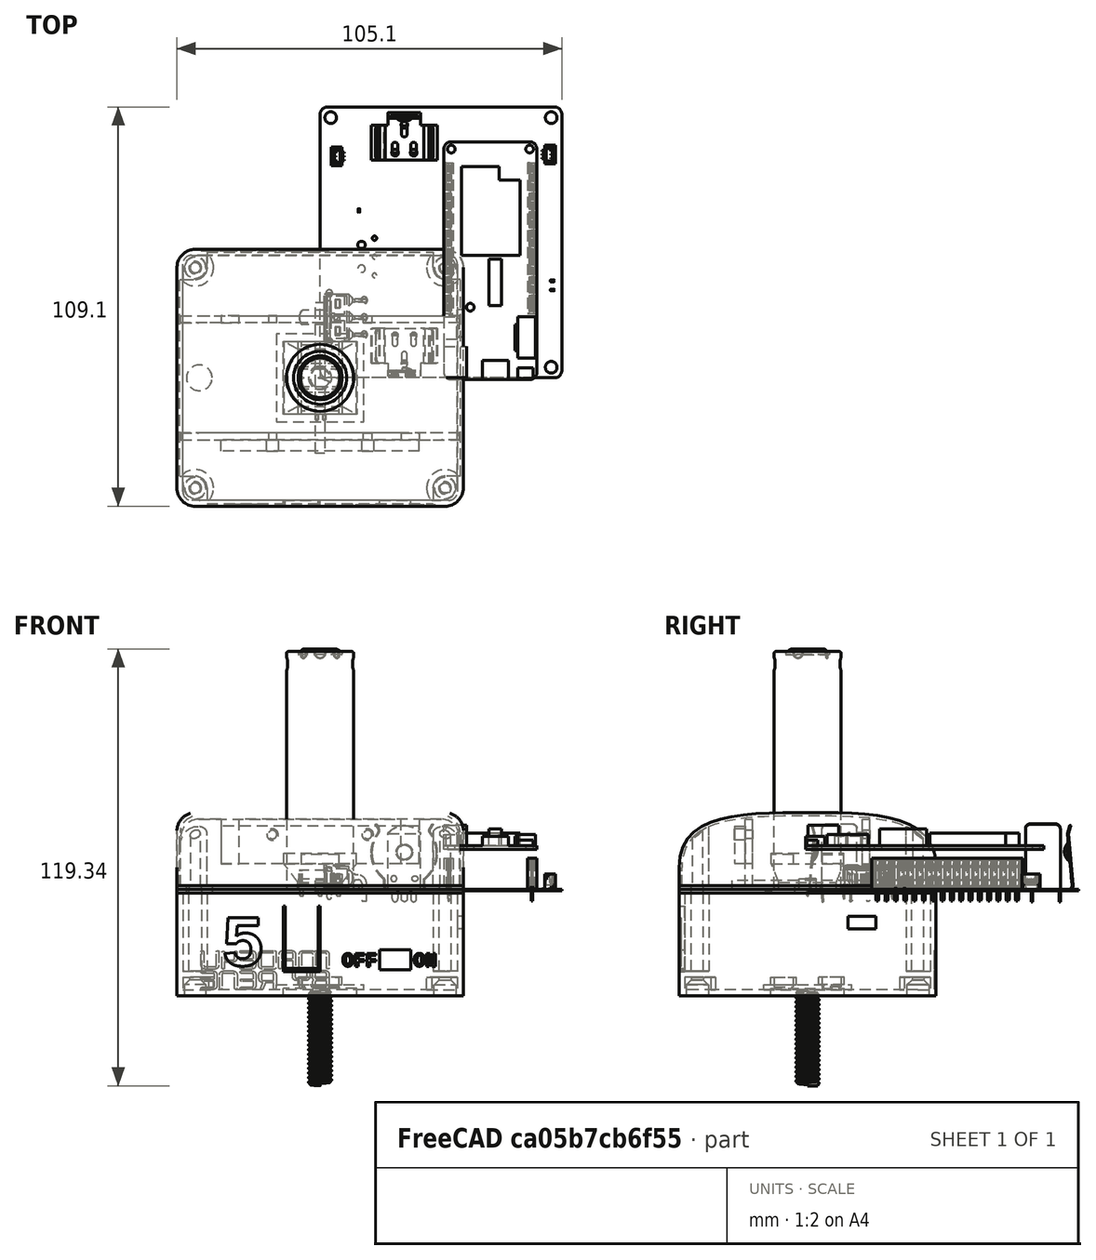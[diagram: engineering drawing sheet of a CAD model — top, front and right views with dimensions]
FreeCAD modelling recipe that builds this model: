
FCSTD DOCUMENT  (FreeCAD 0.20R29177 (Git))
Label: tally_light
License: All rights reserved
LicenseURL: http://en.wikipedia.org/wiki/All_rights_reserved
objects: Sketcher::SketchObject×40, PartDesign::Pocket×22, Part::Feature×20, App::Part×19, PartDesign::Mirrored×14, PartDesign::Pad×13, PartDesign::Body×11, PartDesign::MultiTransform×6, PartDesign::PolarPattern×4, PartDesign::Fillet×4, PartDesign::FeatureBase×2, Spreadsheet::Sheet×1, Mesh::Feature×1, App::DocumentObjectGroup×1, PartDesign::AdditiveLoft×1, Part::Cut×1, Part::MultiCommon×1, PartDesign::Chamfer×1, Part::MultiFuse×1, PartDesign::AdditiveHelix×1, +1 more types
note: 185 computed .brp shape members not serialized (recipe doc carries the construction recipe); baked Part::Feature solids carry a one-line shape summary decoded from their .brp

FEATURE [Spreadsheet::Sheet] Spreadsheet
  cells = A1=Width; B1(width)=78.2; A2=Depth; B2(depth)=70.2; A3=Height; B3(height)=50; A4=Wall Width; B4(wall_width)=1.6; A5=PCB Width; B5(pcb_width)=65; A6=PCB Depth; B6(pcb_depth)=25.6; A8=Light Wall Width; B8(light_wall_width)=0.8; A9=Light Height; B9(light_height)=20
FEATURE [Sketcher::SketchObject] Sketch002
  FullyConstrained = true
  MapMode = 5
  Support = -> [XY_Plane001]
  expr: Constraints[8] = Spreadsheet.depth
  expr: Constraints[9] = Spreadsheet.width
  sketch-geometry (4):
    g0: LineSegment StartX=-39.1 StartY=35.1 StartZ=0 EndX=39.1 EndY=35.1 EndZ=0
    g1: LineSegment StartX=39.1 StartY=35.1 StartZ=0 EndX=39.1 EndY=-35.1 EndZ=0
    g2: LineSegment StartX=39.1 StartY=-35.1 StartZ=0 EndX=-39.1 EndY=-35.1 EndZ=0
    g3: LineSegment StartX=-39.1 StartY=-35.1 StartZ=0 EndX=-39.1 EndY=35.1 EndZ=0
  constraints (11):
    c: Coincident(g0,g1)
    c: Coincident(g1,g2)
    c: Coincident(g2,g3)
    c: Coincident(g3,g0)
    c: Horizontal(g0)
    c: Horizontal(g2)
    c: Vertical(g1)
    c: Vertical(g3)
    c: Distance(g3) = 70.2
    c: Distance(g2) = 78.2
    c: Symmetric(g0,g2,g-1)
FEATURE [PartDesign::Pad] Pad001
  Direction = (0,0,1)
  Length = 1
  Length2 = 10
  Profile = -> Sketch002
  ReferenceAxis = -> Sketch002 [N_Axis]
  Type = 0
FEATURE [Sketcher::SketchObject] Sketch003
  AttachmentOffset = pos=(0,0,1) rot=(0,0,1;0rad)
  FullyConstrained = true
  MapMode = 5
  Placement = pos=(0,0,1) rot=(0,0,1;0rad)
  Support = -> [XY_Plane001]
  expr: Constraints[7] = Spreadsheet.width - 2 * Spreadsheet.light_wall_width - 0.4
  sketch-geometry (4):
    g0: LineSegment StartX=-38.1 StartY=17 StartZ=0 EndX=38.1 EndY=17 EndZ=0
    g1: LineSegment StartX=38.1 StartY=17 StartZ=0 EndX=38.1 EndY=15 EndZ=0
    g2: LineSegment StartX=38.1 StartY=15 StartZ=0 EndX=-38.1 EndY=15 EndZ=0
    g3: LineSegment StartX=-38.1 StartY=15 StartZ=0 EndX=-38.1 EndY=17 EndZ=0
  constraints (11):
    c: Coincident(g0,g1)
    c: Coincident(g1,g2)
    c: Coincident(g2,g3)
    c: Coincident(g3,g0)
    c: Vertical(g1)
    c: Vertical(g3)
    c: Distance(g3) = 2
    c: Distance(g0) = 76.2
    c: Symmetric(g2,g1,g-2)
    c: Distance(g-1,g2) = 15
    c: Horizontal(g0)
FEATURE [PartDesign::Pad] Pad002
  BaseFeature = -> Pad001
  Direction = (0,0,1)
  Length = 18.2
  Length2 = 10
  Profile = -> Sketch003
  ReferenceAxis = -> Sketch003 [N_Axis]
  Type = 0
  expr: Length = Spreadsheet.light_height - Spreadsheet.light_wall_width - 1
FEATURE [Sketcher::SketchObject] Sketch004
  FullyConstrained = true
  MapMode = 5
  Support = -> [XY_Plane002]
  expr: Constraints[17] = Spreadsheet.width
  expr: Constraints[18] = Spreadsheet.depth
  sketch-geometry (8):
    g0: LineSegment StartX=-34.1 StartY=35.1 StartZ=0 EndX=34.1 EndY=35.1 EndZ=0
    g1: LineSegment StartX=39.1 StartY=30.1 StartZ=0 EndX=39.1 EndY=-30.1 EndZ=0
    g2: LineSegment StartX=34.1 StartY=-35.1 StartZ=0 EndX=-34.1 EndY=-35.1 EndZ=0
    g3: LineSegment StartX=-39.1 StartY=-30.1 StartZ=0 EndX=-39.1 EndY=30.1 EndZ=0
    g4: ArcOfCircle CenterX=-34.1 CenterY=30.1 CenterZ=0 NormalX=0 NormalY=0 NormalZ=1 AngleXU=0 Radius=5 StartAngle=1.5708 EndAngle=3.14159
    g5: ArcOfCircle CenterX=34.1 CenterY=30.1 CenterZ=0 NormalX=0 NormalY=0 NormalZ=1 AngleXU=0 Radius=5 StartAngle=0 EndAngle=1.5708
    g6: ArcOfCircle CenterX=34.1 CenterY=-30.1 CenterZ=0 NormalX=0 NormalY=0 NormalZ=1 AngleXU=0 Radius=5 StartAngle=4.71239 EndAngle=6.28319
    g7: ArcOfCircle CenterX=-34.1 CenterY=-30.1 CenterZ=0 NormalX=0 NormalY=0 NormalZ=1 AngleXU=0 Radius=5 StartAngle=3.14159 EndAngle=4.71239
  constraints (19):
    c: Horizontal(g0)
    c: Vertical(g1)
    c: Horizontal(g2)
    c: Vertical(g3)
    c: Vertical(g0,g2)
    c: Vertical(g0,g2)
    c: Horizontal(g1,g3)
    c: Tangent(g2,g7) = 1.5708
    c: Tangent(g3,g7) = 1.5708
    c: Tangent(g0,g4) = 1.5708
    c: Tangent(g3,g4) = 1.5708
    c: Tangent(g0,g5) = 1.5708
    c: Tangent(g1,g5) = 1.5708
    c: Tangent(g1,g6) = 1.5708
    c: Tangent(g2,g6) = 1.5708
    c: Symmetric(g0,g2,g-1)
    c: Diameter(g4) = 10
    c: Distance(g3,g1) = 78.2
    c: Distance(g0,g2) = 70.2
FEATURE [PartDesign::Pad] Pad003
  Direction = (0,0,1)
  Length = 28
  Length2 = 10
  Profile = -> Sketch004
  ReferenceAxis = -> Sketch004 [N_Axis]
  Reversed = true
  Type = 0
  expr: Length = Spreadsheet.height - Spreadsheet.light_height - 2
FEATURE [Sketcher::SketchObject] Sketch006
  FullyConstrained = true
  MapMode = 5
  Support = -> [XY_Plane003]
  expr: Constraints[8] = Spreadsheet.depth
  expr: Constraints[9] = Spreadsheet.width
  sketch-geometry (4):
    g0: LineSegment StartX=-39.1 StartY=35.1 StartZ=0 EndX=39.1 EndY=35.1 EndZ=0
    g1: LineSegment StartX=39.1 StartY=35.1 StartZ=0 EndX=39.1 EndY=-35.1 EndZ=0
    g2: LineSegment StartX=39.1 StartY=-35.1 StartZ=0 EndX=-39.1 EndY=-35.1 EndZ=0
    g3: LineSegment StartX=-39.1 StartY=-35.1 StartZ=0 EndX=-39.1 EndY=35.1 EndZ=0
  constraints (11):
    c: Coincident(g0,g1)
    c: Coincident(g1,g2)
    c: Coincident(g2,g3)
    c: Coincident(g3,g0)
    c: Horizontal(g0)
    c: Horizontal(g2)
    c: Vertical(g1)
    c: Vertical(g3)
    c: Distance(g3) = 70.2
    c: Distance(g2) = 78.2
    c: Symmetric(g0,g2,g-1)
FEATURE [PartDesign::Pad] Pad004
  Direction = (0,0,1)
  Length = 1
  Length2 = 10
  Profile = -> Sketch006
  ReferenceAxis = -> Sketch006 [N_Axis]
  Reversed = true
  Type = 0
FEATURE [Sketcher::SketchObject] Sketch008
  AttachmentOffset = pos=(0,0,-28) rot=(0,0,1;0rad)
  ExternalGeometry = -> [Sketch004]
  FullyConstrained = true
  MapMode = 5
  Placement = pos=(0,0,-28) rot=(0,0,1;0rad)
  Support = -> [XY_Plane002]
  expr: .AttachmentOffset.Base.z = -(Spreadsheet.height - Spreadsheet.light_height - 2)
  sketch-geometry (2):
    g0: Circle CenterX=-34.1 CenterY=30.1 CenterZ=0 NormalX=0 NormalY=0 NormalZ=1 AngleXU=0 Radius=1.6
    g1: Circle CenterX=-34.1 CenterY=30.1 CenterZ=0 NormalX=0 NormalY=0 NormalZ=1 AngleXU=0 Radius=5
  constraints (5):
    c: Diameter(g0) = 3.2
    c: Coincident(g1,g0)
    c: Diameter(g1) = 10
    c: Distance(g-4,g0) = 5
    c: Distance(g0,g-3) = 5
FEATURE [Sketcher::SketchObject] Sketch009
  AttachmentOffset = pos=(0,0,-28) rot=(0,0,1;0rad)
  ExternalGeometry = -> [Pad003]
  FullyConstrained = true
  MapMode = 5
  Placement = pos=(0,0,-28) rot=(0,0,1;0rad)
  Support = -> [XY_Plane002]
  expr: .AttachmentOffset.Base.z = -(Spreadsheet.height - Spreadsheet.light_height) + 2
  sketch-geometry (1):
    g0: Circle CenterX=-34.1 CenterY=30.1 CenterZ=0 NormalX=0 NormalY=0 NormalZ=1 AngleXU=0 Radius=3
  constraints (3):
    c: Diameter(g0) = 6
    c: Distance(g-3,g0) = 5
    c: Distance(g-4,g0) = 5
FEATURE [Sketcher::SketchObject] Sketch010
  FullyConstrained = false
  MapMode = 5
  Support = -> [XY_Plane001]
  sketch-geometry (1):
    g0: Circle CenterX=-34.1 CenterY=30.1 CenterZ=0 NormalX=0 NormalY=0 NormalZ=1 AngleXU=0 Radius=1.6
  constraints (1):
    c: Diameter(g0) = 3.2
FEATURE [PartDesign::Mirrored] Mirrored007
  MirrorPlane = -> Sketch010 [V_Axis]
FEATURE [PartDesign::Mirrored] Mirrored008
  MirrorPlane = -> Sketch010 [H_Axis]
FEATURE [Sketcher::SketchObject] Sketch011
  FullyConstrained = false
  MapMode = 5
  Support = -> [XY_Plane003]
  sketch-geometry (1):
    g0: Circle CenterX=-34.1 CenterY=30.1 CenterZ=0 NormalX=0 NormalY=0 NormalZ=1 AngleXU=0 Radius=1.7
  constraints (1):
    c: Diameter(g0) = 3.4
FEATURE [PartDesign::Pocket] Pocket004
  BaseFeature = -> Pad004
  Direction = (0,0,-1)
  Length = 5
  Length2 = 5
  Midplane = true
  Profile = -> Sketch011
  ReferenceAxis = -> Sketch011 [N_Axis]
  Type = 1
FEATURE [PartDesign::Mirrored] Mirrored009
  MirrorPlane = -> Sketch011 [V_Axis]
FEATURE [PartDesign::Mirrored] Mirrored010
  MirrorPlane = -> Sketch011 [H_Axis]
FEATURE [PartDesign::MultiTransform] MultiTransform003
  BaseFeature = -> Pocket004
  Originals = -> [Pocket004]
  Transformations = -> [Mirrored009,Mirrored010]
FEATURE [Sketcher::SketchObject] Sketch013
  FullyConstrained = true
  MapMode = 5
  Support = -> [XY_Plane001]
  sketch-geometry (1):
    g0: Circle CenterX=-33 CenterY=0 CenterZ=0 NormalX=0 NormalY=0 NormalZ=1 AngleXU=0 Radius=3.5
  constraints (3):
    c: PointOnObject(g0,g-1)
    c: Diameter(g0) = 7
    c: Distance(g0,g-1) = 33
FEATURE [PartDesign::Mirrored] Mirrored011
  MirrorPlane = -> Sketch008 [V_Axis]
FEATURE [PartDesign::Mirrored] Mirrored012
  MirrorPlane = -> Sketch008 [H_Axis]
FEATURE [Sketcher::SketchObject] Sketch015
  FullyConstrained = true
  MapMode = 5
  Support = -> [XY_Plane003]
  expr: Constraints[12] = 5 - Spreadsheet.wall_width
  expr: Constraints[13] = 5 - Spreadsheet.wall_width
  expr: Constraints[14] = Spreadsheet.depth / 2 - 5
  expr: Constraints[15] = Spreadsheet.width / 2 - 5
  expr: Constraints[2] = 3.2 / 2 + Spreadsheet.wall_width
  sketch-geometry (6):
    g0: Circle CenterX=-34.1 CenterY=30.1 CenterZ=0 NormalX=0 NormalY=0 NormalZ=1 AngleXU=0 Radius=1.7
    g1: ArcOfCircle CenterX=-34.1 CenterY=30.1 CenterZ=0 NormalX=0 NormalY=0 NormalZ=1 AngleXU=0 Radius=3.2 StartAngle=4.71239 EndAngle=6.28319
    g2: LineSegment StartX=-30.9 StartY=33.5 StartZ=0 EndX=-37.5 EndY=33.5 EndZ=0
    g3: LineSegment StartX=-37.5 StartY=33.5 StartZ=0 EndX=-37.5 EndY=26.9 EndZ=0
    g4: LineSegment StartX=-30.9 StartY=30.1 StartZ=0 EndX=-30.9 EndY=33.5 EndZ=0
    g5: LineSegment StartX=-37.5 StartY=26.9 StartZ=0 EndX=-34.1 EndY=26.9 EndZ=0
  constraints (16):
    c: Diameter(g0) = 3.4
    c: Coincident(g1,g0)
    c: Radius(g1) = 3.2
    c: Horizontal(g2)
    c: Coincident(g3,g2)
    c: Vertical(g3)
    c: Coincident(g4,g2)
    c: Vertical(g4)
    c: Coincident(g5,g3)
    c: Horizontal(g5)
    c: Tangent(g4,g1) = -1.5708
    c: Tangent(g5,g1) = -1.5708
    c: Distance(g0,g2) = 3.4
    c: Distance(g0,g3) = 3.4
    c: Distance(g0,g-1) = 30.1
    c: Distance(g0,g-2) = 34.1
FEATURE [PartDesign::Pad] Pad008
  BaseFeature = -> MultiTransform003
  Direction = (0,0,1)
  Length = 22.3
  Length2 = 10
  Profile = -> Sketch015
  ReferenceAxis = -> Sketch015 [N_Axis]
  Reversed = true
  Type = 0
  expr: Length = Spreadsheet.height - Spreadsheet.light_height - 2 - 4 - 1.7
FEATURE [PartDesign::Mirrored] Mirrored017
  MirrorPlane = -> Sketch015 [V_Axis]
FEATURE [PartDesign::Mirrored] Mirrored018
  MirrorPlane = -> Sketch015 [H_Axis]
FEATURE [PartDesign::MultiTransform] MultiTransform006
  BaseFeature = -> Pad008
  Originals = -> [Pad008]
  Transformations = -> [Mirrored017,Mirrored018]
FEATURE [Sketcher::SketchObject] Sketch016
  FullyConstrained = true
  MapMode = 5
  Placement = pos=(0,-35.1,0) rot=(1,0,0;1.5708rad)
  Support = -> [Pad003]
  sketch-geometry (4):
    g0: LineSegment StartX=16.25 StartY=-15.5 StartZ=0 EndX=24.75 EndY=-15.5 EndZ=0
    g1: LineSegment StartX=24.75 StartY=-15.5 StartZ=0 EndX=24.75 EndY=-21 EndZ=0
    g2: LineSegment StartX=24.75 StartY=-21 StartZ=0 EndX=16.25 EndY=-21 EndZ=0
    g3: LineSegment StartX=16.25 StartY=-21 StartZ=0 EndX=16.25 EndY=-15.5 EndZ=0
  constraints (12):
    c: Coincident(g0,g1)
    c: Coincident(g1,g2)
    c: Coincident(g2,g3)
    c: Coincident(g3,g0)
    c: Horizontal(g0)
    c: Horizontal(g2)
    c: Vertical(g1)
    c: Vertical(g3)
    c: Distance(g1) = 5.5
    c: Distance(g2) = 8.5
    c: Distance(g0,g-2) = 16.25
    c: Distance(g0,g-1) = 15.5
FEATURE [Sketcher::SketchObject] Sketch017
  FullyConstrained = true
  MapMode = 5
  Placement = pos=(0,-35.1,0) rot=(1,0,0;1.5708rad)
  Support = -> [Pad003]
  sketch-geometry (8):
    g0: LineSegment StartX=-9.5 StartY=-3.5 StartZ=0 EndX=-10 EndY=-3.5 EndZ=0
    g1: LineSegment StartX=-10 StartY=-3.5 StartZ=0 EndX=-10 EndY=-21.5 EndZ=0
    g2: LineSegment StartX=-10 StartY=-21.5 StartZ=0 EndX=0 EndY=-21.5 EndZ=0
    g3: LineSegment StartX=0 StartY=-21.5 StartZ=0 EndX=0 EndY=-3.5 EndZ=0
    g4: LineSegment StartX=0 StartY=-3.5 StartZ=0 EndX=-0.5 EndY=-3.5 EndZ=0
    g5: LineSegment StartX=-0.5 StartY=-3.5 StartZ=0 EndX=-0.5 EndY=-20.5 EndZ=0
    g6: LineSegment StartX=-0.5 StartY=-20.5 StartZ=0 EndX=-9.5 EndY=-20.5 EndZ=0
    g7: LineSegment StartX=-9.5 StartY=-20.5 StartZ=0 EndX=-9.5 EndY=-3.5 EndZ=0
  constraints (24):
    c: Horizontal(g0)
    c: Coincident(g0,g1)
    c: Vertical(g1)
    c: Coincident(g1,g2)
    c: Horizontal(g2)
    c: Coincident(g2,g3)
    c: Vertical(g3)
    c: Coincident(g3,g4)
    c: Horizontal(g4)
    c: Coincident(g4,g5)
    c: Vertical(g5)
    c: Coincident(g5,g6)
    c: Horizontal(g6)
    c: Coincident(g6,g7)
    c: Coincident(g7,g0)
    c: Vertical(g7)
    c: Equal(g0,g4)
    c: Distance(g4) = 0.5
    c: Distance(g6,g2) = 1
    c: Horizontal(g4,g0)
    c: Distance(g5) = 17
    c: Distance(g3,g-1) = 3.5
    c: Distance(g2) = 10
    c: PointOnObject(g2,g-2)
FEATURE [Sketcher::SketchObject] Sketch018
  FullyConstrained = true
  MapMode = 5
  Placement = pos=(39.1,0,0) rot=(0.57735,0.57735,0.57735;2.0944rad)
  Support = -> [Pad003]
  sketch-geometry (4):
    g0: LineSegment StartX=11.1 StartY=-6.3 StartZ=0 EndX=18.6 EndY=-6.3 EndZ=0
    g1: LineSegment StartX=18.6 StartY=-6.3 StartZ=0 EndX=18.6 EndY=-9.8 EndZ=0
    g2: LineSegment StartX=18.6 StartY=-9.8 StartZ=0 EndX=11.1 EndY=-9.8 EndZ=0
    g3: LineSegment StartX=11.1 StartY=-9.8 StartZ=0 EndX=11.1 EndY=-6.3 EndZ=0
  constraints (12):
    c: Coincident(g0,g1)
    c: Coincident(g1,g2)
    c: Coincident(g2,g3)
    c: Coincident(g3,g0)
    c: Horizontal(g0)
    c: Horizontal(g2)
    c: Vertical(g1)
    c: Vertical(g3)
    c: Distance(g0) = 7.5
    c: Distance(g3) = 3.5
    c: Distance(g0,g-1) = 6.3
    c: Distance(g2,g-2) = 11.1
FEATURE [Sketcher::SketchObject] Sketch021
  FullyConstrained = true
  MapMode = 5
  Placement = pos=(0,0,0) rot=(1,0,0;1.5708rad)
  Support = -> [XZ_Plane001]
  expr: Constraints[2] = Spreadsheet.light_height / 2 + 10 / 2
  sketch-geometry (1):
    g0: Circle CenterX=-13 CenterY=15 CenterZ=0 NormalX=0 NormalY=0 NormalZ=1 AngleXU=0 Radius=1.15
  constraints (3):
    c: Diameter(g0) = 2.3
    c: Distance(g0,g-2) = 13
    c: Distance(g0,g-1) = 15
FEATURE [Part::Feature] Part__Feature001  label="Open CASCADE STEP translator 6.8 3.1.1"
  Placement = pos=(0,0,-0.41148) rot=(0,0,1;0rad)
  shape: bbox 66 x 74 x 0.4115 mm, 62 faces (baked)
FEATURE [App::Part] Board
  Group = -> [Part__Feature001]
  Origin = -> Origin004
FEATURE [Part::Feature] Part__Feature002  label="_____C161LFBN-RC"
  Placement = pos=(36.345,17.6,0) rot=(0.57735,0.57735,0.57735;2.0944rad)
  shape: bbox 2.54 x 41.14 x 11.7 mm, 810 faces, 17 solids (baked)
FEATURE [Part::Feature] Part__Feature003  label="_____C161LFBN-RC001"
  Placement = pos=(59.12,17.55,0) rot=(0.57735,0.57735,0.57735;2.0944rad)
  shape: bbox 2.54 x 41.14 x 11.7 mm, 810 faces, 17 solids (baked)
FEATURE [Part::Feature] Part__Feature004  label="wemos_d32_Pro"
  Placement = pos=(33.8,-0.5,11) rot=(0,0,1;0rad)
  shape: bbox 25.4 x 65 x 6.5 mm, 57 faces (baked)
FEATURE [Part::Feature] Part__Feature005  label="Extruded"
  shape: bbox 2.475 x 41.18 x 2.5 mm, 6 faces (baked)
FEATURE [App::Part] _465872176  label="8465872176"
  Group = -> [Part__Feature005]
  Origin = -> Origin005
  Placement = pos=(35.1875,38.1375,8.5) rot=(0,0,1;0rad)
FEATURE [Part::Feature] Part__Feature006  label="Extruded001"
  shape: bbox 2.475 x 41.18 x 2.5 mm, 6 faces (baked)
FEATURE [App::Part] _465872176001  label="8465872176001"
  Group = -> [Part__Feature006]
  Origin = -> Origin006
  Placement = pos=(57.8125,38.1375,8.5) rot=(0,0,1;0rad)
FEATURE [App::Part] U1
  Group = -> [Part__Feature002,Part__Feature003,Part__Feature004,_465872176,_465872176001]
  Origin = -> Origin007
FEATURE [Part::Feature] Part__Feature007  label="500SSPxS2M6xEA"
  Placement = pos=(7.9,16.5,3.3) rot=(-0.57735,-0.57735,0.57735;2.0944rad)
  shape: bbox 18.41 x 13.57 x 9.78 mm, 248 faces (baked)
FEATURE [App::Part] S2
  Group = -> [Part__Feature007]
  Origin = -> Origin008
FEATURE [Part::Feature] Part__Feature008  label="Open CASCADE STEP translator 6.8 3.4.1.1"
  shape: bbox 11.8 x 4.7 x 4.7 mm, 26 faces (baked)
FEATURE [Part::Feature] Part__Feature009  label="Open CASCADE STEP translator 6.8 3.4.1.2"
  shape: bbox 17.1 x 9.6 x 11.72 mm, 133 faces, 0 solids (baked)
FEATURE [App::Part] SS075xx02FxxxV2A
  Group = -> [Part__Feature008,Part__Feature009]
  Origin = -> Origin009
  Placement = pos=(9.75,33.045,2.875) rot=(-0.57735,-0.57735,0.57735;2.0944rad)
FEATURE [App::Part] S1
  Group = -> [SS075xx02FxxxV2A]
  Origin = -> Origin010
FEATURE [Part::Feature] Part__Feature010  label="RES0603"
  Placement = pos=(-0.899935,-10.6999,-0.41148) rot=(0.707107,0.707107,0;3.14159rad)
  shape: bbox 0.8002 x 1.6 x 0.45 mm, 22 faces, 4 solids (baked)
FEATURE [App::Part] R5
  Group = -> [Part__Feature010]
  Origin = -> Origin011
FEATURE [Part::Feature] Part__Feature011  label="RES0604"
  Placement = pos=(1.10007,-10.6999,-0.41148) rot=(0.707107,0.707107,0;3.14159rad)
  shape: bbox 0.8002 x 1.6 x 0.45 mm, 22 faces, 4 solids (baked)
FEATURE [App::Part] R4
  Group = -> [Part__Feature011]
  Origin = -> Origin012
FEATURE [Part::Feature] Part__Feature012  label="RES0402"
  Placement = pos=(63.3999,23.9999,0) rot=(0,0,1;3.14159rad)
  shape: bbox 1 x 0.5 x 0.3 mm, 22 faces, 4 solids (baked)
FEATURE [App::Part] R3
  Group = -> [Part__Feature012]
  Origin = -> Origin013
FEATURE [Part::Feature] Part__Feature013  label="RES0605"
  Placement = pos=(63.3999,26.4999,0) rot=(0,0,1;3.14159rad)
  shape: bbox 1 x 0.5 x 0.3 mm, 22 faces, 4 solids (baked)
FEATURE [App::Part] R2
  Group = -> [Part__Feature013]
  Origin = -> Origin014
FEATURE [Part::Feature] Part__Feature014  label="RES0606"
  Placement = pos=(10.5999,45.7001,0) rot=(0,0,1;1.5708rad)
  shape: bbox 0.5 x 1 x 0.3 mm, 22 faces, 4 solids (baked)
FEATURE [App::Part] R1
  Group = -> [Part__Feature014]
  Origin = -> Origin015
FEATURE [Part::Feature] Part__Feature015  label="BM03B-SRSS-TB"
  Placement = pos=(63.525,61.0001,0) rot=(0.57735,-0.57735,-0.57735;2.0944rad)
  shape: bbox 3.6 x 5 x 4.32 mm, 82 faces (baked)
FEATURE [App::Part] J2
  Group = -> [Part__Feature015]
  Origin = -> Origin016
FEATURE [Part::Feature] Part__Feature016  label="BM03B-SRSS-TB001"
  Placement = pos=(3.70004,60.4999,0) rot=(0.57735,0.57735,0.57735;2.0944rad)
  shape: bbox 3.6 x 5 x 4.32 mm, 82 faces (baked)
FEATURE [App::Part] J1
  Group = -> [Part__Feature016]
  Origin = -> Origin017
FEATURE [Part::Feature] Part__Feature017  label="keystone-PN54"
  Placement = pos=(23,13.5,0) rot=(0.57735,-0.57735,-0.57735;2.0944rad)
  shape: bbox 18.1 x 13.01 x 21.35 mm, 123 faces (baked)
FEATURE [Part::Feature] Part__Feature018  label="keystone-PN055"
  Placement = pos=(23,59.5,0) rot=(0.57735,0.57735,0.57735;2.0944rad)
  shape: bbox 18.1 x 13.01 x 21.35 mm, 123 faces (baked)
FEATURE [Part::Feature] Part__Feature019  label="Top_cover_v1"
  Placement = pos=(-1e-15,-2.09268e-05,65.7015) rot=(1,0,0;3.14159rad)
  shape: bbox 11.91 x 11.91 x 2.501 mm, 63 faces (baked)
FEATURE [Part::Feature] Part__Feature020  label="Open CASCADE STEP translator 6.8 3.12.3.2"
  shape: bbox 20.46 x 20.46 x 65 mm, 19 faces (baked)
FEATURE [App::Part] INR18650_35E  label="INR18650-35E"
  Group = -> [Part__Feature019,Part__Feature020]
  Origin = -> Origin018
  Placement = pos=(23,69,9.5) rot=(1,0,0;1.5708rad)
FEATURE [App::Part] BT1
  Group = -> [Part__Feature017,Part__Feature018,INR18650_35E]
  Origin = -> Origin019
FEATURE [App::Part] PCB  label="PCB001"
  Group = -> [Board,U1,S2,S1,R5,R4,R3,R2,R1,J2,J1,BT1]
  Origin = -> Origin020
  Placement = pos=(37,-33,-22.4) rot=(0,0,1;1.5708rad)
FEATURE [PartDesign::Mirrored] Mirrored013
  MirrorPlane = -> Sketch009 [V_Axis]
FEATURE [PartDesign::Mirrored] Mirrored014
  MirrorPlane = -> Sketch009 [H_Axis]
FEATURE [PartDesign::Mirrored] Mirrored023
  BaseFeature = -> Pad002
  MirrorPlane = -> Sketch003 [H_Axis]
  Originals = -> [Pad002]
FEATURE [PartDesign::Pocket] Pocket003
  BaseFeature = -> Mirrored023
  Direction = (0,0,-1)
  Length = 5
  Length2 = 5
  Midplane = true
  Profile = -> Sketch010
  ReferenceAxis = -> Sketch010 [N_Axis]
  Type = 1
FEATURE [PartDesign::MultiTransform] MultiTransform002
  BaseFeature = -> Pocket003
  Originals = -> [Pocket003]
  Transformations = -> [Mirrored007,Mirrored008]
FEATURE [PartDesign::Pocket] Pocket006
  BaseFeature = -> MultiTransform002
  Direction = (0,0,-1)
  Length = 5
  Length2 = 5
  Midplane = true
  Profile = -> Sketch013
  ReferenceAxis = -> Sketch013 [N_Axis]
  Type = 0
FEATURE [PartDesign::Pocket] Pocket012
  BaseFeature = -> Pocket006
  Direction = (0,1,2e-16)
  Length = 5
  Length2 = 5
  Midplane = true
  Profile = -> Sketch021
  ReferenceAxis = -> Sketch021 [N_Axis]
  Type = 1
FEATURE [Sketcher::SketchObject] Sketch023
  FullyConstrained = true
  MapMode = 5
  Support = -> [XY_Plane003]
  sketch-geometry (1):
    g0: Circle CenterX=-33 CenterY=0 CenterZ=0 NormalX=0 NormalY=0 NormalZ=1 AngleXU=0 Radius=3.5
  constraints (3):
    c: PointOnObject(g0,g-1)
    c: Diameter(g0) = 7
    c: Distance(g0,g-1) = 33
FEATURE [PartDesign::Pocket] Pocket014
  BaseFeature = -> MultiTransform006
  Direction = (0,0,-1)
  Length = 5
  Length2 = 5
  Profile = -> Sketch023
  ReferenceAxis = -> Sketch023 [N_Axis]
  Type = 0
FEATURE [PartDesign::Mirrored] Mirrored022
  BaseFeature = -> Pocket012
  MirrorPlane = -> Sketch021 [V_Axis]
  Originals = -> [Pocket012]
FEATURE [Sketcher::SketchObject] Sketch024
  FullyConstrained = true
  MapMode = 5
  Placement = pos=(0,0,0) rot=(1,0,0;1.5708rad)
  Support = -> [XZ_Plane001]
  expr: Constraints[8] = 54.2 / 2
  sketch-geometry (4):
    g0: LineSegment StartX=22.1 StartY=20 StartZ=0 EndX=27.1 EndY=20 EndZ=0
    g1: LineSegment StartX=27.1 StartY=20 StartZ=0 EndX=27.1 EndY=7 EndZ=0
    g2: LineSegment StartX=27.1 StartY=7 StartZ=0 EndX=22.1 EndY=7 EndZ=0
    g3: LineSegment StartX=22.1 StartY=7 StartZ=0 EndX=22.1 EndY=20 EndZ=0
  constraints (12):
    c: Coincident(g0,g1)
    c: Coincident(g1,g2)
    c: Coincident(g2,g3)
    c: Coincident(g3,g0)
    c: Horizontal(g0)
    c: Horizontal(g2)
    c: Vertical(g1)
    c: Vertical(g3)
    c: Distance(g0,g-2) = 27.1
    c: Distance(g0) = 5
    c: Distance(g1) = 13
    c: Distance(g0,g-1) = 20
FEATURE [PartDesign::Pocket] Pocket015
  BaseFeature = -> Mirrored022
  Direction = (0,1,2e-16)
  Length = 5
  Length2 = 5
  Profile = -> Sketch024
  ReferenceAxis = -> Sketch024 [N_Axis]
  Reversed = true
  Type = 1
FEATURE [PartDesign::PolarPattern] PolarPattern
  Angle = 360
  Axis = -> Sketch024 [V_Axis]
  BaseFeature = -> Pocket015
  Occurrences = 2
  Originals = -> [Pocket015]
FEATURE [Sketcher::SketchObject] Sketch025
  FullyConstrained = true
  MapMode = 5
  Placement = pos=(0,0,0) rot=(1,0,0;1.5708rad)
  Support = -> [XZ_Plane021]
  sketch-geometry (6):
    g0: LineSegment StartX=-27.1 StartY=5.05 StartZ=0 EndX=27.1 EndY=5.05 EndZ=0
    g1: LineSegment StartX=27.1 StartY=5.05 StartZ=0 EndX=27.1 EndY=-5.05 EndZ=0
    g2: LineSegment StartX=27.1 StartY=-5.05 StartZ=0 EndX=-27.1 EndY=-5.05 EndZ=0
    g3: LineSegment StartX=-27.1 StartY=-5.05 StartZ=0 EndX=-27.1 EndY=5.05 EndZ=0
    g4: Circle CenterX=-13 CenterY=2.75 CenterZ=0 NormalX=0 NormalY=0 NormalZ=1 AngleXU=0 Radius=1.55
    g5: Circle CenterX=13 CenterY=2.75 CenterZ=0 NormalX=0 NormalY=0 NormalZ=1 AngleXU=0 Radius=1.55
  constraints (16):
    c: Coincident(g0,g1)
    c: Coincident(g1,g2)
    c: Coincident(g2,g3)
    c: Coincident(g3,g0)
    c: Horizontal(g0)
    c: Horizontal(g2)
    c: Vertical(g1)
    c: Vertical(g3)
    c: Distance(g1) = 10.1
    c: Distance(g0) = 54.2
    c: Distance(g4,g2) = 7.8
    c: Diameter(g4) = 3.1
    c: Diameter(g5) = 3.1
    c: Distance(g5,g4) = 26
    c: Symmetric(g4,g5,g-2)
    c: Symmetric(g2,g0,g-1)
FEATURE [PartDesign::Pad] Pad010
  Direction = (0,-1,2e-16)
  Length = 3
  Length2 = 10
  Placement = pos=(0,0,0) rot=(1,0,0;1.5708rad)
  Profile = -> Sketch025
  ReferenceAxis = -> Sketch025 [N_Axis]
  Type = 0
FEATURE [PartDesign::Body] Body004  label="LEDFront"
  Group = -> [Sketch025,Pad010]
  Origin = -> Origin021
  Placement = pos=(0,20,12.25) rot=(0,0,1;0rad)
  Tip = -> Pad010
FEATURE [PartDesign::FeatureBase] Clone
  BaseFeature = -> Body004
  Placement = pos=(0,20,12.25) rot=(0,0,1;0rad)
FEATURE [PartDesign::Body] Body005  label="LEDBack"
  BaseFeature = -> Body004
  Group = -> [Clone]
  Origin = -> Origin022
  Placement = pos=(0,0,0) rot=(0,0,1;3.14159rad)
  Tip = -> Clone
FEATURE [Sketcher::SketchObject] Sketch026
  AttachmentOffset = pos=(0,0,-28) rot=(0,0,1;0rad)
  FullyConstrained = true
  MapMode = 5
  Placement = pos=(0,0,-28) rot=(0,0,1;0rad)
  Support = -> [XY_Plane002]
  expr: .AttachmentOffset.Base.z = -(Spreadsheet.height - Spreadsheet.light_height - 2)
  sketch-geometry (4):
    g0: LineSegment StartX=-12 StartY=12 StartZ=0 EndX=12 EndY=12 EndZ=0
    g1: LineSegment StartX=12 StartY=12 StartZ=0 EndX=12 EndY=-12 EndZ=0
    g2: LineSegment StartX=12 StartY=-12 StartZ=0 EndX=-12 EndY=-12 EndZ=0
    g3: LineSegment StartX=-12 StartY=-12 StartZ=0 EndX=-12 EndY=12 EndZ=0
  constraints (11):
    c: Coincident(g0,g1)
    c: Coincident(g1,g2)
    c: Coincident(g2,g3)
    c: Coincident(g3,g0)
    c: Horizontal(g0)
    c: Horizontal(g2)
    c: Vertical(g1)
    c: Vertical(g3)
    c: Equal(g0,g1)
    c: Symmetric(g0,g2,g-1)
    c: Distance(g1) = 24
FEATURE [Sketcher::SketchObject] Sketch027
  AttachmentOffset = pos=(0,0,-28) rot=(0,0,1;0rad)
  FullyConstrained = true
  MapMode = 5
  Placement = pos=(0,0,-28) rot=(0,0,1;0rad)
  Support = -> [XY_Plane002]
  expr: .AttachmentOffset.Base.z = -(Spreadsheet.height - Spreadsheet.light_height - 2)
  sketch-geometry (4):
    g0: LineSegment StartX=-10 StartY=10 StartZ=0 EndX=10 EndY=10 EndZ=0
    g1: LineSegment StartX=10 StartY=10 StartZ=0 EndX=10 EndY=-10 EndZ=0
    g2: LineSegment StartX=10 StartY=-10 StartZ=0 EndX=-10 EndY=-10 EndZ=0
    g3: LineSegment StartX=-10 StartY=-10 StartZ=0 EndX=-10 EndY=10 EndZ=0
  constraints (11):
    c: Coincident(g0,g1)
    c: Coincident(g1,g2)
    c: Coincident(g2,g3)
    c: Coincident(g3,g0)
    c: Horizontal(g0)
    c: Horizontal(g2)
    c: Vertical(g1)
    c: Vertical(g3)
    c: Equal(g0,g1)
    c: Symmetric(g0,g2,g-1)
    c: Distance(g1) = 20
FEATURE [Sketcher::SketchObject] Sketch028
  AttachmentOffset = pos=(0,0,-25) rot=(0,0,1;0rad)
  FullyConstrained = true
  MapMode = 5
  Placement = pos=(0,0,-25) rot=(0,0,1;0rad)
  Support = -> [XY_Plane002]
  expr: .AttachmentOffset.Base.z = -(Spreadsheet.height - Spreadsheet.light_height - 2) + 3
  sketch-geometry (4):
    g0: LineSegment StartX=-6 StartY=-3 StartZ=0 EndX=6 EndY=-3 EndZ=0
    g1: LineSegment StartX=6 StartY=-3 StartZ=0 EndX=6 EndY=-10 EndZ=0
    g2: LineSegment StartX=6 StartY=-10 StartZ=0 EndX=-6 EndY=-10 EndZ=0
    g3: LineSegment StartX=-6 StartY=-10 StartZ=0 EndX=-6 EndY=-3 EndZ=0
  constraints (11):
    c: Coincident(g0,g1)
    c: Coincident(g1,g2)
    c: Coincident(g2,g3)
    c: Coincident(g3,g0)
    c: Horizontal(g2)
    c: Vertical(g1)
    c: Vertical(g3)
    c: Distance(g1) = 7
    c: Distance(g-1,g2) = 10
    c: Distance(g0) = 12
    c: Symmetric(g0,g0,g-2)
FEATURE [Sketcher::SketchObject] Sketch029
  AttachmentOffset = pos=(0,0,-23) rot=(0,0,1;0rad)
  FullyConstrained = true
  MapMode = 5
  Placement = pos=(0,0,-23) rot=(0,0,1;0rad)
  Support = -> [XY_Plane002]
  expr: .AttachmentOffset.Base.z = -(Spreadsheet.height - Spreadsheet.light_height - 2) + 5
  sketch-geometry (4):
    g0: LineSegment StartX=-5.1 StartY=-3.9 StartZ=0 EndX=5.1 EndY=-3.9 EndZ=0
    g1: LineSegment StartX=5.1 StartY=-3.9 StartZ=0 EndX=5.1 EndY=-9.1 EndZ=0
    g2: LineSegment StartX=5.1 StartY=-9.1 StartZ=0 EndX=-5.1 EndY=-9.1 EndZ=0
    g3: LineSegment StartX=-5.1 StartY=-9.1 StartZ=0 EndX=-5.1 EndY=-3.9 EndZ=0
  constraints (11):
    c: Coincident(g0,g1)
    c: Coincident(g1,g2)
    c: Coincident(g2,g3)
    c: Coincident(g3,g0)
    c: Horizontal(g2)
    c: Vertical(g1)
    c: Vertical(g3)
    c: Distance(g1) = 5.2
    c: Distance(g-1,g2) = 9.1
    c: Distance(g0) = 10.2
    c: Symmetric(g0,g0,g-2)
FEATURE [Mesh::Feature] Sony_camera_flash_shoe_insert
  Placement = pos=(-10.5,8.85,-2) rot=(1,0,0;1.5708rad)
  expr: .Placement.Base.x = -21 / 2
  expr: .Placement.Base.y = 15.7 / 2 + 1
FEATURE [App::DocumentObjectGroup] Group  label="Electronics"
  Group = -> [PCB,Body004,Body005]
FEATURE [Sketcher::SketchObject] Sketch030
  FullyConstrained = true
  MapMode = 5
  Support = -> [XY_Plane025]
  sketch-geometry (4):
    g0: LineSegment StartX=-6.1 StartY=-7.85 StartZ=0 EndX=6.1 EndY=-7.85 EndZ=0
    g1: LineSegment StartX=6.1 StartY=-7.85 StartZ=0 EndX=6.1 EndY=7.85 EndZ=0
    g2: LineSegment StartX=6.1 StartY=7.85 StartZ=0 EndX=-6.1 EndY=7.85 EndZ=0
    g3: LineSegment StartX=-6.1 StartY=7.85 StartZ=0 EndX=-6.1 EndY=-7.85 EndZ=0
  constraints (11):
    c: Coincident(g0,g1)
    c: Coincident(g1,g2)
    c: Coincident(g2,g3)
    c: Coincident(g3,g0)
    c: Horizontal(g0)
    c: Horizontal(g2)
    c: Vertical(g1)
    c: Vertical(g3)
    c: Distance(g3) = 15.7
    c: Distance(g2) = 12.2
    c: Symmetric(g2,g0,g-1)
FEATURE [Sketcher::SketchObject] Sketch031
  AttachmentOffset = pos=(0,0,2) rot=(0,0,1;0rad)
  FullyConstrained = true
  MapMode = 5
  Placement = pos=(0,0,2) rot=(0,0,1;0rad)
  Support = -> [XY_Plane025]
  sketch-geometry (4):
    g0: LineSegment StartX=-6.1 StartY=-7.85 StartZ=0 EndX=6.1 EndY=-7.85 EndZ=0
    g1: LineSegment StartX=6.1 StartY=-7.85 StartZ=0 EndX=6.1 EndY=7.85 EndZ=0
    g2: LineSegment StartX=6.1 StartY=7.85 StartZ=0 EndX=-6.1 EndY=7.85 EndZ=0
    g3: LineSegment StartX=-6.1 StartY=7.85 StartZ=0 EndX=-6.1 EndY=-7.85 EndZ=0
  constraints (11):
    c: Coincident(g0,g1)
    c: Coincident(g1,g2)
    c: Coincident(g2,g3)
    c: Coincident(g3,g0)
    c: Horizontal(g0)
    c: Horizontal(g2)
    c: Vertical(g1)
    c: Vertical(g3)
    c: Distance(g3) = 15.7
    c: Distance(g2) = 12.2
    c: Symmetric(g2,g0,g-1)
FEATURE [Sketcher::SketchObject] Sketch032
  AttachmentOffset = pos=(0,0,7) rot=(0,0,1;0rad)
  FullyConstrained = true
  MapMode = 5
  Placement = pos=(0,0,7) rot=(0,0,1;0rad)
  Support = -> [XY_Plane025]
  sketch-geometry (4):
    g0: LineSegment StartX=-9.9 StartY=-9.9 StartZ=0 EndX=9.9 EndY=-9.9 EndZ=0
    g1: LineSegment StartX=9.9 StartY=-9.9 StartZ=0 EndX=9.9 EndY=9.9 EndZ=0
    g2: LineSegment StartX=9.9 StartY=9.9 StartZ=0 EndX=-9.9 EndY=9.9 EndZ=0
    g3: LineSegment StartX=-9.9 StartY=9.9 StartZ=0 EndX=-9.9 EndY=-9.9 EndZ=0
  constraints (11):
    c: Coincident(g0,g1)
    c: Coincident(g1,g2)
    c: Coincident(g2,g3)
    c: Coincident(g3,g0)
    c: Horizontal(g0)
    c: Horizontal(g2)
    c: Vertical(g1)
    c: Vertical(g3)
    c: Distance(g3) = 19.8
    c: Distance(g2) = 19.8
    c: Symmetric(g2,g0,g-1)
FEATURE [Sketcher::SketchObject] Sketch033
  AttachmentOffset = pos=(0,0,10) rot=(0,0,1;0rad)
  FullyConstrained = true
  MapMode = 5
  Placement = pos=(0,0,10) rot=(0,0,1;0rad)
  Support = -> [XY_Plane025]
  sketch-geometry (4):
    g0: LineSegment StartX=-9.9 StartY=-9.9 StartZ=0 EndX=9.9 EndY=-9.9 EndZ=0
    g1: LineSegment StartX=9.9 StartY=-9.9 StartZ=0 EndX=9.9 EndY=9.9 EndZ=0
    g2: LineSegment StartX=9.9 StartY=9.9 StartZ=0 EndX=-9.9 EndY=9.9 EndZ=0
    g3: LineSegment StartX=-9.9 StartY=9.9 StartZ=0 EndX=-9.9 EndY=-9.9 EndZ=0
  constraints (11):
    c: Coincident(g0,g1)
    c: Coincident(g1,g2)
    c: Coincident(g2,g3)
    c: Coincident(g3,g0)
    c: Horizontal(g0)
    c: Horizontal(g2)
    c: Vertical(g1)
    c: Vertical(g3)
    c: Distance(g3) = 19.8
    c: Distance(g2) = 19.8
    c: Symmetric(g2,g0,g-1)
FEATURE [PartDesign::AdditiveLoft] AdditiveLoft
  Closed = false
  Profile = -> Sketch030
  Ruled = true
  Sections = -> [Sketch031,Sketch032,Sketch033]
FEATURE [Sketcher::SketchObject] Sketch034
  AttachmentOffset = pos=(0,0,9.5) rot=(0,0,1;0rad)
  FullyConstrained = true
  MapMode = 5
  Placement = pos=(0,0,9.5) rot=(0,0,1;0rad)
  Support = -> [XY_Plane025]
  sketch-geometry (4):
    g0: LineSegment StartX=-5.1 StartY=-3.9 StartZ=0 EndX=5.1 EndY=-3.9 EndZ=0
    g1: LineSegment StartX=5.1 StartY=-3.9 StartZ=0 EndX=5.1 EndY=-19.1 EndZ=0
    g2: LineSegment StartX=5.1 StartY=-19.1 StartZ=0 EndX=-5.1 EndY=-19.1 EndZ=0
    g3: LineSegment StartX=-5.1 StartY=-19.1 StartZ=0 EndX=-5.1 EndY=-3.9 EndZ=0
  constraints (11):
    c: Coincident(g0,g1)
    c: Coincident(g1,g2)
    c: Coincident(g2,g3)
    c: Coincident(g3,g0)
    c: Horizontal(g2)
    c: Vertical(g1)
    c: Vertical(g3)
    c: Distance(g1) = 15.2
    c: Distance(g-1,g2) = 19.1
    c: Distance(g0) = 10.2
    c: Symmetric(g0,g0,g-2)
FEATURE [PartDesign::Pocket] Pocket018
  BaseFeature = -> AdditiveLoft
  Direction = (0,0,-1)
  Length = 2.5
  Length2 = 5
  Profile = -> Sketch034
  ReferenceAxis = -> Sketch034 [N_Axis]
  Type = 0
FEATURE [PartDesign::PolarPattern] PolarPattern003
  Angle = 360
  Axis = -> Sketch034 [N_Axis]
  BaseFeature = -> Pocket018
  Occurrences = 2
  Originals = -> [Pocket018]
FEATURE [PartDesign::Body] Body006  label="MagnetAdapter"
  Group = -> [Sketch030,Sketch031,Sketch032,AdditiveLoft,Sketch033,Sketch034,Pocket018,PolarPattern003]
  Origin = -> Origin025
  Tip = -> PolarPattern003
FEATURE [App::Part] Part001  label="HotShoeHolder"
  Group = -> [Body006,Sony_camera_flash_shoe_insert]
  Origin = -> Origin024
  Placement = pos=(0,0,-38) rot=(0,0,1;0rad)
FEATURE [Sketcher::SketchObject] Sketch035
  FullyConstrained = true
  MapMode = 5
  Placement = pos=(0,0,0) rot=(0.57735,0.57735,0.57735;2.0944rad)
  expr: Constraints[28] = Spreadsheet.light_height
  expr: Constraints[7] = Spreadsheet.depth
  sketch-geometry (12):
    g0: LineSegment StartX=-35.1 StartY=5 StartZ=0 EndX=-35.1 EndY=0 EndZ=0
    g1: LineSegment StartX=-35.1 StartY=0 StartZ=0 EndX=35.1 EndY=0 EndZ=0
    g2: LineSegment StartX=35.1 StartY=0 StartZ=0 EndX=35.1 EndY=5 EndZ=0
    g3-g7: Circle x5 (B-spline internal-alignment scaffolding for g8; pole/knot coordinates omitted)
    g8: BSplineCurve PolesCount=5 KnotsCount=3 Degree=3 IsPeriodic=0
    g9: GeomPoint X=-35.1 Y=5 Z=0
    g10: GeomPoint X=0 Y=20 Z=0
    g11: GeomPoint X=35.1 Y=5 Z=0
  constraints (26):
    c: PointOnObject(g0,g-1)
    c: Coincident(g0,g1)
    c: Coincident(g1,g2)
    c: Vertical(g2)
    c: Vertical(g0)
    c: Horizontal(g2,g0)
    c: Distance(g2) = 5
    c: Distance(g1) = 70.2
    c: Weight(g3) = 1
    c: Coincident(g8,g0)
    c: Equal(g3,g4)
    c: Equal(g3,g5)
    c: PointOnObject(g5,g-2)
    c: Equal(g3,g6)
    c: Equal(g3,g7)
    c: Coincident(g8,g2)
    c: InternalAlignment(g3-g7 -> g8) x5
    c: InternalAlignment(g9,g8)
    c: InternalAlignment(g10,g8)
    c: InternalAlignment(g11,g8)
    c: Vertical(g4,g0)
    c: Vertical(g6,g2)
    c: Horizontal(g6,g5)
    c: Horizontal(g5,g4)
    c: Distance(g5,g-1) = 20
    c: Symmetric(g0,g1,g-1)
FEATURE [PartDesign::Pad] Pad013
  Direction = (1,0,0)
  Length = 78.2
  Length2 = 10
  Midplane = true
  Placement = pos=(0,0,0) rot=(0.57735,0.57735,0.57735;2.0944rad)
  Profile = -> Sketch035
  ReferenceAxis = -> Sketch035 [N_Axis]
  Type = 0
  expr: Length = Spreadsheet.width
FEATURE [PartDesign::Fillet] Fillet
  Base = -> Pad013 [Edge12,Edge11]
  BaseFeature = -> Pad013
  Placement = pos=(0,0,0) rot=(0.57735,0.57735,0.57735;2.0944rad)
  Radius = 5
  SupportTransform = false
  UseAllEdges = false
FEATURE [PartDesign::Body] Body007  label="LightCoverOuter"
  Group = -> [Sketch035,Pad013,Fillet]
  Origin = -> Origin026
  Placement = pos=(0,0,1) rot=(0,0,1;0rad)
  Tip = -> Fillet
FEATURE [Sketcher::SketchObject] Sketch036
  FullyConstrained = true
  MapMode = 5
  Placement = pos=(0,0,0) rot=(0.57735,0.57735,0.57735;2.0944rad)
  expr: Constraints[28] = Spreadsheet.light_height - Spreadsheet.light_wall_width
  expr: Constraints[7] = Spreadsheet.depth - 2 * Spreadsheet.light_wall_width
  sketch-geometry (12):
    g0: LineSegment StartX=-34.3 StartY=5 StartZ=0 EndX=-34.3 EndY=0 EndZ=0
    g1: LineSegment StartX=-34.3 StartY=0 StartZ=0 EndX=34.3 EndY=0 EndZ=0
    g2: LineSegment StartX=34.3 StartY=0 StartZ=0 EndX=34.3 EndY=5 EndZ=0
    g3-g7: Circle x5 (B-spline internal-alignment scaffolding for g8; pole/knot coordinates omitted)
    g8: BSplineCurve PolesCount=5 KnotsCount=3 Degree=3 IsPeriodic=0
    g9: GeomPoint X=-34.3 Y=5 Z=0
    g10: GeomPoint X=0 Y=19.2 Z=0
    g11: GeomPoint X=34.3 Y=5 Z=0
  constraints (26):
    c: PointOnObject(g0,g-1)
    c: Coincident(g0,g1)
    c: Coincident(g1,g2)
    c: Vertical(g2)
    c: Vertical(g0)
    c: Horizontal(g2,g0)
    c: Distance(g2) = 5
    c: Distance(g1) = 68.6
    c: Weight(g3) = 1
    c: Coincident(g8,g0)
    c: Equal(g3,g4)
    c: Equal(g3,g5)
    c: PointOnObject(g5,g-2)
    c: Equal(g3,g6)
    c: Equal(g3,g7)
    c: Coincident(g8,g2)
    c: InternalAlignment(g3-g7 -> g8) x5
    c: InternalAlignment(g9,g8)
    c: InternalAlignment(g10,g8)
    c: InternalAlignment(g11,g8)
    c: Vertical(g4,g0)
    c: Vertical(g6,g2)
    c: Horizontal(g6,g5)
    c: Horizontal(g5,g4)
    c: Distance(g5,g-1) = 19.2
    c: Symmetric(g0,g1,g-1)
FEATURE [PartDesign::Pad] Pad014
  Direction = (1,0,0)
  Length = 76.6
  Length2 = 10
  Midplane = true
  Placement = pos=(0,0,0) rot=(0.57735,0.57735,0.57735;2.0944rad)
  Profile = -> Sketch036
  ReferenceAxis = -> Sketch036 [N_Axis]
  Type = 0
  expr: Length = Spreadsheet.width - 2 * Spreadsheet.light_wall_width
FEATURE [PartDesign::Fillet] Fillet001
  Base = -> Pad014 [Edge12,Edge11]
  BaseFeature = -> Pad014
  Placement = pos=(0,0,0) rot=(0.57735,0.57735,0.57735;2.0944rad)
  Radius = 5
  SupportTransform = false
  UseAllEdges = false
FEATURE [PartDesign::Body] Body008  label="LightCoverInner"
  Group = -> [Sketch036,Pad014,Fillet001]
  Origin = -> Origin027
  Placement = pos=(0,0,1) rot=(0,0,1;0rad)
  Tip = -> Fillet001
FEATURE [PartDesign::FeatureBase] Clone001
  BaseFeature = -> Body008
  Placement = pos=(0,0,1) rot=(0,0,1;0rad)
FEATURE [PartDesign::Body] Body009  label="LightCoverInnerCut"
  BaseFeature = -> Body008
  Group = -> [Clone001]
  Origin = -> Origin028
  Tip = -> Clone001
FEATURE [Part::Cut] Cut
  Base = -> Body007
  Tool = -> Body008
FEATURE [Sketcher::SketchObject] Sketch037
  FullyConstrained = true
  MapMode = 5
  Support = -> [XY_Plane027]
  expr: Constraints[10] = Spreadsheet.depth
  expr: Constraints[20] = Spreadsheet.light_wall_width
  expr: Constraints[21] = Spreadsheet.light_wall_width
  expr: Constraints[9] = Spreadsheet.width
  sketch-geometry (8):
    g0: LineSegment StartX=-39.1 StartY=35.1 StartZ=0 EndX=39.1 EndY=35.1 EndZ=0
    g1: LineSegment StartX=39.1 StartY=35.1 StartZ=0 EndX=39.1 EndY=-35.1 EndZ=0
    g2: LineSegment StartX=39.1 StartY=-35.1 StartZ=0 EndX=-39.1 EndY=-35.1 EndZ=0
    g3: LineSegment StartX=-39.1 StartY=-35.1 StartZ=0 EndX=-39.1 EndY=35.1 EndZ=0
    g4: LineSegment StartX=-38.3 StartY=34.3 StartZ=0 EndX=38.3 EndY=34.3 EndZ=0
    g5: LineSegment StartX=38.3 StartY=34.3 StartZ=0 EndX=38.3 EndY=-34.3 EndZ=0
    g6: LineSegment StartX=38.3 StartY=-34.3 StartZ=0 EndX=-38.3 EndY=-34.3 EndZ=0
    g7: LineSegment StartX=-38.3 StartY=-34.3 StartZ=0 EndX=-38.3 EndY=34.3 EndZ=0
  constraints (22):
    c: Coincident(g0,g1)
    c: Coincident(g1,g2)
    c: Coincident(g2,g3)
    c: Coincident(g3,g0)
    c: Horizontal(g0)
    c: Horizontal(g2)
    c: Vertical(g1)
    c: Vertical(g3)
    c: Symmetric(g1,g0,g-1)
    c: Distance(g0) = 78.2
    c: Distance(g1) = 70.2
    c: Coincident(g4,g5)
    c: Coincident(g5,g6)
    c: Coincident(g6,g7)
    c: Coincident(g7,g4)
    c: Horizontal(g4)
    c: Horizontal(g6)
    c: Vertical(g5)
    c: Vertical(g7)
    c: Symmetric(g4,g6,g-1)
    c: Distance(g4,g1) = 0.8
    c: Distance(g4,g0) = 0.8
FEATURE [PartDesign::Pad] Pad015
  Direction = (0,0,1)
  Length = 5
  Length2 = 10
  Profile = -> Sketch037
  ReferenceAxis = -> Sketch037 [N_Axis]
  Type = 0
FEATURE [Sketcher::SketchObject] Sketch038
  FullyConstrained = true
  MapMode = 5
  Support = -> [XY_Plane027]
  expr: Constraints[12] = 5 - Spreadsheet.light_wall_width
  expr: Constraints[13] = 5 - Spreadsheet.light_wall_width
  expr: Constraints[14] = Spreadsheet.depth / 2 - 5
  expr: Constraints[15] = Spreadsheet.width / 2 - 5
  expr: Constraints[2] = 3.2 / 2 + Spreadsheet.wall_width
  sketch-geometry (6):
    g0: Circle CenterX=-34.1 CenterY=30.1 CenterZ=0 NormalX=0 NormalY=0 NormalZ=1 AngleXU=0 Radius=1.4
    g1: ArcOfCircle CenterX=-34.1 CenterY=30.1 CenterZ=0 NormalX=0 NormalY=0 NormalZ=1 AngleXU=0 Radius=3.2 StartAngle=4.71239 EndAngle=6.28319
    g2: LineSegment StartX=-30.9 StartY=34.3 StartZ=0 EndX=-38.3 EndY=34.3 EndZ=0
    g3: LineSegment StartX=-38.3 StartY=34.3 StartZ=0 EndX=-38.3 EndY=26.9 EndZ=0
    g4: LineSegment StartX=-30.9 StartY=30.1 StartZ=0 EndX=-30.9 EndY=34.3 EndZ=0
    g5: LineSegment StartX=-38.3 StartY=26.9 StartZ=0 EndX=-34.1 EndY=26.9 EndZ=0
  constraints (16):
    c: Diameter(g0) = 2.8
    c: Coincident(g1,g0)
    c: Radius(g1) = 3.2
    c: Horizontal(g2)
    c: Coincident(g3,g2)
    c: Vertical(g3)
    c: Coincident(g4,g2)
    c: Vertical(g4)
    c: Coincident(g5,g3)
    c: Horizontal(g5)
    c: Tangent(g4,g1) = -1.5708
    c: Tangent(g5,g1) = -1.5708
    c: Distance(g0,g2) = 4.2
    c: Distance(g0,g3) = 4.2
    c: Distance(g0,g-1) = 30.1
    c: Distance(g0,g-2) = 34.1
FEATURE [PartDesign::Pad] Pad016
  BaseFeature = -> Pad015
  Direction = (0,0,1)
  Length = 20
  Length2 = 10
  Profile = -> Sketch038
  ReferenceAxis = -> Sketch038 [N_Axis]
  Type = 0
  expr: Length = Spreadsheet.light_height
FEATURE [PartDesign::Mirrored] Mirrored024
  MirrorPlane = -> Sketch038 [V_Axis]
FEATURE [PartDesign::Mirrored] Mirrored025
  MirrorPlane = -> Sketch038 [H_Axis]
FEATURE [PartDesign::MultiTransform] MultiTransform008
  BaseFeature = -> Pad016
  Originals = -> [Pad016]
  Transformations = -> [Mirrored024,Mirrored025]
FEATURE [PartDesign::Body] Body010
  Group = -> [Sketch037,Pad015,Sketch038,Pad016,MultiTransform008,Mirrored024,Mirrored025]
  Origin = -> Origin029
  Tip = -> MultiTransform008
FEATURE [Part::MultiCommon] Common
  Shapes = -> [Body010,Body009]
FEATURE [PartDesign::Fillet] Fillet002
  Base = -> PolarPattern [Edge58,Edge46,Edge5,Edge1,Edge2,Edge75,Edge8,Edge48]
  BaseFeature = -> PolarPattern
  Radius = 5
  SupportTransform = false
  UseAllEdges = false
FEATURE [PartDesign::Body] Body001  label="LedHolder"
  Group = -> [Sketch002,Pad001,Sketch003,Pad002,Mirrored023,Sketch010,Pocket003,MultiTransform002,Mirrored007,Mirrored008,Sketch013,Pocket006,Sketch021,Pocket012,Mirrored022,Sketch024,Pocket015,PolarPattern,Fillet002]
  Origin = -> Origin001
  Tip = -> Fillet002
FEATURE [PartDesign::Fillet] Fillet003
  Base = -> Pocket014 [Edge97,Edge2,Edge78,Edge8,Edge5,Edge67,Edge88,Edge1]
  BaseFeature = -> Pocket014
  Radius = 5
  SupportTransform = false
  UseAllEdges = false
FEATURE [PartDesign::Body] Body003  label="ElectronicsHolder"
  Group = -> [Sketch006,Pad004,Sketch011,Pocket004,MultiTransform003,Mirrored009,Mirrored010,Sketch015,Pad008,MultiTransform006,Mirrored017,Mirrored018,Sketch023,Pocket014,Fillet003]
  Origin = -> Origin003
  Tip = -> Fillet003
FEATURE [Sketcher::SketchObject] Sketch039
  FullyConstrained = true
  MapMode = 5
  Support = -> [XY_Plane002]
  expr: Constraints[17] = Spreadsheet.depth - 2 * Spreadsheet.wall_width
  expr: Constraints[18] = Spreadsheet.width - 2 * Spreadsheet.wall_width
  sketch-geometry (8):
    g0: LineSegment StartX=-32.5 StartY=33.5 StartZ=0 EndX=32.5 EndY=33.5 EndZ=0
    g1: LineSegment StartX=37.5 StartY=28.5 StartZ=0 EndX=37.5 EndY=-28.5 EndZ=0
    g2: LineSegment StartX=32.5 StartY=-33.5 StartZ=0 EndX=-32.5 EndY=-33.5 EndZ=0
    g3: LineSegment StartX=-37.5 StartY=-28.5 StartZ=0 EndX=-37.5 EndY=28.5 EndZ=0
    g4: ArcOfCircle CenterX=-32.5 CenterY=28.5 CenterZ=0 NormalX=0 NormalY=0 NormalZ=1 AngleXU=0 Radius=5 StartAngle=1.5708 EndAngle=3.14159
    g5: ArcOfCircle CenterX=32.5 CenterY=28.5 CenterZ=0 NormalX=0 NormalY=0 NormalZ=1 AngleXU=0 Radius=5 StartAngle=0 EndAngle=1.5708
    g6: ArcOfCircle CenterX=32.5 CenterY=-28.5 CenterZ=0 NormalX=0 NormalY=0 NormalZ=1 AngleXU=0 Radius=5 StartAngle=4.71239 EndAngle=6.28319
    g7: ArcOfCircle CenterX=-32.5 CenterY=-28.5 CenterZ=0 NormalX=0 NormalY=0 NormalZ=1 AngleXU=0 Radius=5 StartAngle=3.14159 EndAngle=4.71239
  constraints (19):
    c: Horizontal(g0)
    c: Vertical(g1)
    c: Horizontal(g2)
    c: Vertical(g3)
    c: Vertical(g0,g2)
    c: Vertical(g0,g2)
    c: Horizontal(g1,g3)
    c: Tangent(g2,g7) = 1.5708
    c: Tangent(g3,g7) = 1.5708
    c: Tangent(g0,g4) = 1.5708
    c: Tangent(g3,g4) = 1.5708
    c: Tangent(g0,g5) = 1.5708
    c: Tangent(g1,g5) = 1.5708
    c: Tangent(g1,g6) = 1.5708
    c: Tangent(g2,g6) = 1.5708
    c: Symmetric(g0,g2,g-1)
    c: Diameter(g4) = 10
    c: Distance(g0,g2) = 67
    c: Distance(g3,g1) = 75
FEATURE [PartDesign::Pocket] Pocket
  BaseFeature = -> Pad003
  Direction = (0,0,-1)
  Length = 0
  Length2 = 5
  Offset = -1.6
  Profile = -> Sketch039
  ReferenceAxis = -> Sketch039 [N_Axis]
  Type = 3
  UpToFace = -> Pad003 [Face10]
  expr: Offset = -Spreadsheet.wall_width
FEATURE [PartDesign::Pad] Pad006
  BaseFeature = -> Pocket
  Direction = (0,0,1)
  Length = 5
  Length2 = 10
  Profile = -> Sketch008
  ReferenceAxis = -> Sketch008 [N_Axis]
  Type = 0
FEATURE [PartDesign::MultiTransform] MultiTransform004
  BaseFeature = -> Pad006
  Originals = -> [Pad006]
  Transformations = -> [Mirrored011,Mirrored012]
FEATURE [PartDesign::Pocket] Pocket007
  BaseFeature = -> MultiTransform004
  Direction = (0,0,-1)
  Length = 3
  Length2 = 5
  Profile = -> Sketch009
  ReferenceAxis = -> Sketch009 [N_Axis]
  Reversed = true
  Type = 0
FEATURE [PartDesign::MultiTransform] MultiTransform
  BaseFeature = -> Pocket007
  Originals = -> [Pocket007]
  Transformations = -> [Mirrored013,Mirrored014]
FEATURE [PartDesign::Pocket] Pocket010
  BaseFeature = -> MultiTransform
  Direction = (-1,0,0)
  Length = 1.6
  Length2 = 5
  Profile = -> Sketch018
  ReferenceAxis = -> Sketch018 [N_Axis]
  Type = 0
  expr: Length = Spreadsheet.wall_width
FEATURE [PartDesign::Pocket] Pocket008
  BaseFeature = -> Pocket010
  Direction = (0,1,-2e-16)
  Length = 1.6
  Length2 = 5
  Profile = -> Sketch016
  ReferenceAxis = -> Sketch016 [N_Axis]
  Type = 0
  expr: Length = Spreadsheet.wall_width
FEATURE [PartDesign::Pocket] Pocket009
  BaseFeature = -> Pocket008
  Direction = (0,1,-2e-16)
  Length = 1.6
  Length2 = 5
  Profile = -> Sketch017
  ReferenceAxis = -> Sketch017 [N_Axis]
  Type = 0
  expr: Length = Spreadsheet.wall_width
FEATURE [PartDesign::Pad] Pad011
  BaseFeature = -> Pocket009
  Direction = (0,0,1)
  Length = 3
  Length2 = 10
  Profile = -> Sketch026
  ReferenceAxis = -> Sketch026 [N_Axis]
  Type = 0
FEATURE [PartDesign::Pocket] Pocket016
  BaseFeature = -> Pad011
  Direction = (0,0,-1)
  Length = 2
  Length2 = 5
  Profile = -> Sketch027
  ReferenceAxis = -> Sketch027 [N_Axis]
  Reversed = true
  Type = 0
FEATURE [PartDesign::Pad] Pad012
  BaseFeature = -> Pocket016
  Direction = (0,0,1)
  Length = 2
  Length2 = 10
  Profile = -> Sketch028
  ReferenceAxis = -> Sketch028 [N_Axis]
  Type = 0
FEATURE [PartDesign::PolarPattern] PolarPattern001
  Angle = 360
  Axis = -> Sketch028 [N_Axis]
  BaseFeature = -> Pad012
  Occurrences = 2
  Originals = -> [Pad012]
FEATURE [PartDesign::Pocket] Pocket017
  BaseFeature = -> PolarPattern001
  Direction = (0,0,-1)
  Length = 2.6
  Length2 = 5
  Profile = -> Sketch029
  ReferenceAxis = -> Sketch029 [N_Axis]
  Type = 0
FEATURE [PartDesign::PolarPattern] PolarPattern002
  Angle = 360
  Axis = -> Sketch029 [N_Axis]
  BaseFeature = -> Pocket017
  Occurrences = 2
  Originals = -> [Pocket017]
FEATURE [PartDesign::Chamfer] Chamfer
  Angle = 45
  Base = -> PolarPattern002 [Edge190,Edge189,Edge192,Edge202]
  BaseFeature = -> PolarPattern002
  ChamferType = 0
  FlipDirection = false
  Size = 1.3
  Size2 = 1
  SupportTransform = false
  UseAllEdges = false
FEATURE [Part::MultiFuse] Fusion  label="LightCover"
  Shapes = -> [Common,Cut]
FEATURE [Sketcher::SketchObject] Sketch
  FullyConstrained = true
  MapMode = 5
  Support = -> [XY_Plane002]
  expr: Constraints[15] = Spreadsheet.width - Spreadsheet.wall_width * 2
  expr: Constraints[16] = Spreadsheet.depth - Spreadsheet.wall_width * 2
  sketch-geometry (8):
    g0: LineSegment StartX=-35 StartY=33.5 StartZ=0 EndX=35 EndY=33.5 EndZ=0
    g1: LineSegment StartX=37.5 StartY=31 StartZ=0 EndX=37.5 EndY=-31 EndZ=0
    g2: LineSegment StartX=35 StartY=-33.5 StartZ=0 EndX=-35 EndY=-33.5 EndZ=0
    g3: LineSegment StartX=-37.5 StartY=-31 StartZ=0 EndX=-37.5 EndY=31 EndZ=0
    g4: ArcOfCircle CenterX=-35 CenterY=31 CenterZ=0 NormalX=0 NormalY=0 NormalZ=1 AngleXU=0 Radius=2.5 StartAngle=1.5708 EndAngle=3.14159
    g5: ArcOfCircle CenterX=35 CenterY=31 CenterZ=0 NormalX=0 NormalY=0 NormalZ=1 AngleXU=0 Radius=2.5 StartAngle=0 EndAngle=1.5708
    g6: ArcOfCircle CenterX=35 CenterY=-31 CenterZ=0 NormalX=0 NormalY=0 NormalZ=1 AngleXU=0 Radius=2.5 StartAngle=4.71239 EndAngle=6.28319
    g7: ArcOfCircle CenterX=-35 CenterY=-31 CenterZ=0 NormalX=0 NormalY=0 NormalZ=1 AngleXU=0 Radius=2.5 StartAngle=3.14159 EndAngle=4.71239
  constraints (19):
    c: Horizontal(g0)
    c: Vertical(g1)
    c: Horizontal(g2)
    c: Vertical(g3)
    c: Tangent(g3,g4) = 1.5708
    c: Tangent(g0,g4) = 1.5708
    c: Tangent(g0,g5) = 1.5708
    c: Tangent(g1,g5) = 1.5708
    c: Tangent(g1,g6) = 1.5708
    c: Tangent(g2,g6) = 1.5708
    c: Tangent(g2,g7) = 1.5708
    c: Tangent(g3,g7) = 1.5708
    c: Equal(g7,g6)
    c: Equal(g6,g5)
    c: Equal(g5,g4)
    c: Distance(g3,g1) = 75
    c: Distance(g0,g2) = 67
    c: Symmetric(g0,g2,g-1)
    c: Diameter(g4) = 5
FEATURE [PartDesign::Pocket] Pocket019
  BaseFeature = -> Chamfer
  Direction = (0,0,-1)
  Length = 23
  Length2 = 5
  Profile = -> Sketch
  ReferenceAxis = -> Sketch [N_Axis]
  Type = 0
FEATURE [Sketcher::SketchObject] Sketch040
  FullyConstrained = false
  Placement = pos=(0,-35.1,1) rot=(1,0,0;1.5708rad)
  expr: .Placement.Base.y = -Spreadsheet.depth / 2
  sketch-geometry (70):
    g0: BSplineCurve PolesCount=3 KnotsCount=2 Degree=2 IsPeriodic=0
    g1: BSplineCurve PolesCount=3 KnotsCount=2 Degree=2 IsPeriodic=0
    g2: BSplineCurve PolesCount=3 KnotsCount=2 Degree=2 IsPeriodic=0
    g3: BSplineCurve PolesCount=3 KnotsCount=2 Degree=2 IsPeriodic=0
    g4: BSplineCurve PolesCount=3 KnotsCount=2 Degree=2 IsPeriodic=0
    g5: BSplineCurve PolesCount=3 KnotsCount=2 Degree=2 IsPeriodic=0
    g6: BSplineCurve PolesCount=3 KnotsCount=2 Degree=2 IsPeriodic=0
    g7: BSplineCurve PolesCount=3 KnotsCount=2 Degree=2 IsPeriodic=0
    g8: BSplineCurve PolesCount=3 KnotsCount=2 Degree=2 IsPeriodic=0
    g9: BSplineCurve PolesCount=3 KnotsCount=2 Degree=2 IsPeriodic=0
    g10: BSplineCurve PolesCount=3 KnotsCount=2 Degree=2 IsPeriodic=0
    g11: BSplineCurve PolesCount=3 KnotsCount=2 Degree=2 IsPeriodic=0
    g12: BSplineCurve PolesCount=3 KnotsCount=2 Degree=2 IsPeriodic=0
    g13: BSplineCurve PolesCount=3 KnotsCount=2 Degree=2 IsPeriodic=0
    g14: BSplineCurve PolesCount=3 KnotsCount=2 Degree=2 IsPeriodic=0
    g15: BSplineCurve PolesCount=3 KnotsCount=2 Degree=2 IsPeriodic=0
    g16: LineSegment StartX=30.6345 StartY=-21 StartZ=0 EndX=29.6414 EndY=-18.3466 EndZ=0
    g17: LineSegment StartX=31.5293 StartY=-21 StartZ=0 EndX=30.6345 EndY=-21 EndZ=0
    g18: LineSegment StartX=31.5293 StartY=-17.469 StartZ=0 EndX=31.5293 EndY=-21 EndZ=0
    g19: LineSegment StartX=30.8655 StartY=-17.469 StartZ=0 EndX=31.5293 EndY=-17.469 EndZ=0
    g20: LineSegment StartX=30.8655 StartY=-19.2345 StartZ=0 EndX=30.8655 EndY=-17.469 EndZ=0
    g21: BSplineCurve PolesCount=3 KnotsCount=2 Degree=2 IsPeriodic=0
    g22: BSplineCurve PolesCount=3 KnotsCount=2 Degree=2 IsPeriodic=0
    g23: BSplineCurve PolesCount=3 KnotsCount=2 Degree=2 IsPeriodic=0
    g24: LineSegment StartX=29.9207 StartY=-17.469 StartZ=0 EndX=30.9379 EndY=-20.1931 EndZ=0
    g25: LineSegment StartX=29.05 StartY=-17.469 StartZ=0 EndX=29.9207 EndY=-17.469 EndZ=0
    g26: LineSegment StartX=29.05 StartY=-21 StartZ=0 EndX=29.05 EndY=-17.469 EndZ=0
    g27: LineSegment StartX=29.7138 StartY=-21 StartZ=0 EndX=29.05 EndY=-21 EndZ=0
    g28: LineSegment StartX=29.7138 StartY=-19.2759 StartZ=0 EndX=29.7138 EndY=-21 EndZ=0
    g29: BSplineCurve PolesCount=3 KnotsCount=2 Degree=2 IsPeriodic=0
    g30: BSplineCurve PolesCount=3 KnotsCount=2 Degree=2 IsPeriodic=0
    g31: BSplineCurve PolesCount=3 KnotsCount=2 Degree=2 IsPeriodic=0
    g32: BSplineCurve PolesCount=3 KnotsCount=2 Degree=2 IsPeriodic=0
    g33: BSplineCurve PolesCount=3 KnotsCount=2 Degree=2 IsPeriodic=0
    g34: BSplineCurve PolesCount=3 KnotsCount=2 Degree=2 IsPeriodic=0
    g35: BSplineCurve PolesCount=3 KnotsCount=2 Degree=2 IsPeriodic=0
    g36: BSplineCurve PolesCount=3 KnotsCount=2 Degree=2 IsPeriodic=0
    g37: BSplineCurve PolesCount=3 KnotsCount=2 Degree=2 IsPeriodic=0
    g38: BSplineCurve PolesCount=3 KnotsCount=2 Degree=2 IsPeriodic=0
    g39: BSplineCurve PolesCount=3 KnotsCount=2 Degree=2 IsPeriodic=0
    g40: BSplineCurve PolesCount=3 KnotsCount=2 Degree=2 IsPeriodic=0
    g41: BSplineCurve PolesCount=3 KnotsCount=2 Degree=2 IsPeriodic=0
    g42: BSplineCurve PolesCount=3 KnotsCount=2 Degree=2 IsPeriodic=0
    g43: BSplineCurve PolesCount=3 KnotsCount=2 Degree=2 IsPeriodic=0
    g44: BSplineCurve PolesCount=3 KnotsCount=2 Degree=2 IsPeriodic=0
    g45: BSplineCurve PolesCount=3 KnotsCount=2 Degree=2 IsPeriodic=0
    g46: BSplineCurve PolesCount=3 KnotsCount=2 Degree=2 IsPeriodic=0
    g47: BSplineCurve PolesCount=3 KnotsCount=2 Degree=2 IsPeriodic=0
    g48: BSplineCurve PolesCount=3 KnotsCount=2 Degree=2 IsPeriodic=0
    g49: BSplineCurve PolesCount=3 KnotsCount=2 Degree=2 IsPeriodic=0
    g50: LineSegment StartX=10.3948 StartY=-18.0207 StartZ=0 EndX=10.3948 EndY=-19.1241 EndZ=0
    g51: LineSegment StartX=12.0603 StartY=-18.0207 StartZ=0 EndX=10.3948 EndY=-18.0207 EndZ=0
    g52: LineSegment StartX=12.0603 StartY=-17.469 StartZ=0 EndX=12.0603 EndY=-18.0207 EndZ=0
    g53: LineSegment StartX=9.63276 StartY=-17.469 StartZ=0 EndX=12.0603 EndY=-17.469 EndZ=0
    g54: LineSegment StartX=9.63276 StartY=-21 StartZ=0 EndX=9.63276 EndY=-17.469 EndZ=0
    g55: LineSegment StartX=10.3948 StartY=-21 StartZ=0 EndX=9.63276 EndY=-21 EndZ=0
    g56: LineSegment StartX=10.3948 StartY=-19.6759 StartZ=0 EndX=10.3948 EndY=-21 EndZ=0
    g57: LineSegment StartX=12.0017 StartY=-19.6759 StartZ=0 EndX=10.3948 EndY=-19.6759 EndZ=0
    g58: LineSegment StartX=12.0017 StartY=-19.1241 StartZ=0 EndX=12.0017 EndY=-19.6759 EndZ=0
    g59: LineSegment StartX=10.3948 StartY=-19.1241 StartZ=0 EndX=12.0017 EndY=-19.1241 EndZ=0
    g60: LineSegment StartX=13.5948 StartY=-18.0207 StartZ=0 EndX=13.5948 EndY=-19.1241 EndZ=0
    g61: LineSegment StartX=15.2603 StartY=-18.0207 StartZ=0 EndX=13.5948 EndY=-18.0207 EndZ=0
    g62: LineSegment StartX=15.2603 StartY=-17.469 StartZ=0 EndX=15.2603 EndY=-18.0207 EndZ=0
    g63: LineSegment StartX=12.8328 StartY=-17.469 StartZ=0 EndX=15.2603 EndY=-17.469 EndZ=0
    g64: LineSegment StartX=12.8328 StartY=-21 StartZ=0 EndX=12.8328 EndY=-17.469 EndZ=0
    g65: LineSegment StartX=13.5948 StartY=-21 StartZ=0 EndX=12.8328 EndY=-21 EndZ=0
    g66: LineSegment StartX=13.5948 StartY=-19.6759 StartZ=0 EndX=13.5948 EndY=-21 EndZ=0
    g67: LineSegment StartX=15.2017 StartY=-19.6759 StartZ=0 EndX=13.5948 EndY=-19.6759 EndZ=0
    g68: LineSegment StartX=15.2017 StartY=-19.1241 StartZ=0 EndX=15.2017 EndY=-19.6759 EndZ=0
    g69: LineSegment StartX=13.5948 StartY=-19.1241 StartZ=0 EndX=15.2017 EndY=-19.1241 EndZ=0
  constraints (98):
    c: Coincident(g0,g1)
    c: Coincident(g1,g2)
    c: Coincident(g2,g3)
    c: Coincident(g3,g4)
    c: Coincident(g4,g5)
    c: Coincident(g5,g6)
    c: Coincident(g6,g7)
    c: Coincident(g7,g0)
    c: Coincident(g8,g9)
    c: Coincident(g9,g10)
    c: Coincident(g10,g11)
    c: Coincident(g11,g12)
    c: Coincident(g12,g13)
    c: Coincident(g13,g14)
    c: Coincident(g14,g15)
    c: Coincident(g15,g8)
    c: Coincident(g16,g17)
    c: Horizontal(g17)
    c: Coincident(g17,g18)
    c: Vertical(g18)
    c: Coincident(g18,g19)
    c: Horizontal(g19)
    c: Coincident(g19,g20)
    c: Vertical(g20)
    c: Coincident(g20,g21)
    c: Coincident(g21,g22)
    c: Coincident(g22,g23)
    c: Coincident(g23,g24)
    c: Coincident(g24,g25)
    c: Horizontal(g25)
    c: Coincident(g25,g26)
    c: Vertical(g26)
    c: Coincident(g26,g27)
    c: Horizontal(g27)
    c: Coincident(g27,g28)
    c: Vertical(g28)
    c: Coincident(g28,g29)
    c: Coincident(g29,g30)
    c: Coincident(g30,g31)
    c: Coincident(g31,g32)
    c: Coincident(g32,g33)
    c: Coincident(g33,g16)
    c: Coincident(g34,g35)
    c: Coincident(g35,g36)
    c: Coincident(g36,g37)
    c: Coincident(g37,g38)
    c: Coincident(g38,g39)
    c: Coincident(g39,g40)
    c: Coincident(g40,g41)
    c: Coincident(g41,g34)
    c: Coincident(g42,g43)
    c: Coincident(g43,g44)
    c: Coincident(g44,g45)
    c: Coincident(g45,g46)
    c: Coincident(g46,g47)
    c: Coincident(g47,g48)
    c: Coincident(g48,g49)
    c: Coincident(g49,g42)
    c: Vertical(g50)
    c: Coincident(g50,g51)
    c: Horizontal(g51)
    c: Coincident(g51,g52)
    c: Vertical(g52)
    c: Coincident(g52,g53)
    c: Horizontal(g53)
    c: Coincident(g53,g54)
    c: Vertical(g54)
    c: Coincident(g54,g55)
    c: Horizontal(g55)
    c: Coincident(g55,g56)
    c: Vertical(g56)
    c: Coincident(g56,g57)
    c: Horizontal(g57)
    c: Coincident(g57,g58)
    c: Vertical(g58)
    c: Coincident(g58,g59)
    c: Horizontal(g59)
    c: Coincident(g59,g50)
    c: Vertical(g60)
    c: Coincident(g60,g61)
    c: Horizontal(g61)
    c: Coincident(g61,g62)
    c: Vertical(g62)
    c: Coincident(g62,g63)
    c: Horizontal(g63)
    c: Coincident(g63,g64)
    c: Vertical(g64)
    c: Coincident(g64,g65)
    c: Horizontal(g65)
    c: Coincident(g65,g66)
    c: Vertical(g66)
    c: Coincident(g66,g67)
    c: Horizontal(g67)
    c: Coincident(g67,g68)
    c: Vertical(g68)
    c: Coincident(g68,g69)
    c: Horizontal(g69)
    c: Coincident(g69,g60)
FEATURE [PartDesign::Pocket] Pocket020
  BaseFeature = -> Pocket019
  Direction = (0,1,-2e-16)
  Length = 0.4
  Length2 = 5
  Profile = -> Sketch040
  ReferenceAxis = -> Sketch040 [N_Axis]
  Type = 0
FEATURE [Sketcher::SketchObject] Sketch041
  FullyConstrained = false
  Placement = pos=(-15,35.1,-21) rot=(0,0.707107,0.707107;3.14159rad)
  expr: .Placement.Base.y = Spreadsheet.depth / 2
  sketch-geometry (225):
    g0: BSplineCurve PolesCount=4 KnotsCount=2 Degree=3 IsPeriodic=0
    g1: BSplineCurve PolesCount=4 KnotsCount=2 Degree=3 IsPeriodic=0
    g2: BSplineCurve PolesCount=2 KnotsCount=2 Degree=1 IsPeriodic=0
    g3: BSplineCurve PolesCount=4 KnotsCount=2 Degree=3 IsPeriodic=0
    g4: BSplineCurve PolesCount=2 KnotsCount=2 Degree=1 IsPeriodic=0
    g5: BSplineCurve PolesCount=4 KnotsCount=2 Degree=3 IsPeriodic=0
    g6: BSplineCurve PolesCount=4 KnotsCount=2 Degree=3 IsPeriodic=0
    g7: BSplineCurve PolesCount=2 KnotsCount=2 Degree=1 IsPeriodic=0
    g8: BSplineCurve PolesCount=4 KnotsCount=2 Degree=3 IsPeriodic=0
    g9: BSplineCurve PolesCount=2 KnotsCount=2 Degree=1 IsPeriodic=0
    g10: BSplineCurve PolesCount=4 KnotsCount=2 Degree=3 IsPeriodic=0
    g11: BSplineCurve PolesCount=2 KnotsCount=2 Degree=1 IsPeriodic=0
    g12: BSplineCurve PolesCount=4 KnotsCount=2 Degree=3 IsPeriodic=0
    g13: BSplineCurve PolesCount=4 KnotsCount=2 Degree=3 IsPeriodic=0
    g14: BSplineCurve PolesCount=2 KnotsCount=2 Degree=1 IsPeriodic=0
    g15: BSplineCurve PolesCount=4 KnotsCount=2 Degree=3 IsPeriodic=0
    g16: BSplineCurve PolesCount=2 KnotsCount=2 Degree=1 IsPeriodic=0
    g17: BSplineCurve PolesCount=4 KnotsCount=2 Degree=3 IsPeriodic=0
    g18: BSplineCurve PolesCount=2 KnotsCount=2 Degree=1 IsPeriodic=0
    g19: BSplineCurve PolesCount=4 KnotsCount=2 Degree=3 IsPeriodic=0
    g20: BSplineCurve PolesCount=4 KnotsCount=2 Degree=3 IsPeriodic=0
    g21: BSplineCurve PolesCount=2 KnotsCount=2 Degree=1 IsPeriodic=0
    g22: BSplineCurve PolesCount=4 KnotsCount=2 Degree=3 IsPeriodic=0
    g23: BSplineCurve PolesCount=2 KnotsCount=2 Degree=1 IsPeriodic=0
    g24: BSplineCurve PolesCount=4 KnotsCount=2 Degree=3 IsPeriodic=0
    g25: BSplineCurve PolesCount=2 KnotsCount=2 Degree=1 IsPeriodic=0
    g26: BSplineCurve PolesCount=4 KnotsCount=2 Degree=3 IsPeriodic=0
    g27: BSplineCurve PolesCount=4 KnotsCount=2 Degree=3 IsPeriodic=0
    g28: BSplineCurve PolesCount=2 KnotsCount=2 Degree=1 IsPeriodic=0
    g29: BSplineCurve PolesCount=2 KnotsCount=2 Degree=1 IsPeriodic=0
    g30: BSplineCurve PolesCount=2 KnotsCount=2 Degree=1 IsPeriodic=0
    g31: BSplineCurve PolesCount=4 KnotsCount=2 Degree=3 IsPeriodic=0
    g32: BSplineCurve PolesCount=4 KnotsCount=2 Degree=3 IsPeriodic=0
    g33: BSplineCurve PolesCount=2 KnotsCount=2 Degree=1 IsPeriodic=0
    g34: BSplineCurve PolesCount=4 KnotsCount=2 Degree=3 IsPeriodic=0
    g35: BSplineCurve PolesCount=2 KnotsCount=2 Degree=1 IsPeriodic=0
    g36: BSplineCurve PolesCount=4 KnotsCount=2 Degree=3 IsPeriodic=0
    g37: BSplineCurve PolesCount=2 KnotsCount=2 Degree=1 IsPeriodic=0
    g38: BSplineCurve PolesCount=4 KnotsCount=2 Degree=3 IsPeriodic=0
    g39: BSplineCurve PolesCount=2 KnotsCount=2 Degree=1 IsPeriodic=0
    g40: BSplineCurve PolesCount=2 KnotsCount=2 Degree=1 IsPeriodic=0
    g41: BSplineCurve PolesCount=2 KnotsCount=2 Degree=1 IsPeriodic=0
    g42: BSplineCurve PolesCount=4 KnotsCount=2 Degree=3 IsPeriodic=0
    g43: BSplineCurve PolesCount=2 KnotsCount=2 Degree=1 IsPeriodic=0
    g44: BSplineCurve PolesCount=4 KnotsCount=2 Degree=3 IsPeriodic=0
    g45: BSplineCurve PolesCount=2 KnotsCount=2 Degree=1 IsPeriodic=0
    g46: BSplineCurve PolesCount=4 KnotsCount=2 Degree=3 IsPeriodic=0
    g47: BSplineCurve PolesCount=2 KnotsCount=2 Degree=1 IsPeriodic=0
    g48: BSplineCurve PolesCount=4 KnotsCount=2 Degree=3 IsPeriodic=0
    g49: BSplineCurve PolesCount=2 KnotsCount=2 Degree=1 IsPeriodic=0
    g50: BSplineCurve PolesCount=4 KnotsCount=2 Degree=3 IsPeriodic=0
    g51: BSplineCurve PolesCount=2 KnotsCount=2 Degree=1 IsPeriodic=0
    g52: BSplineCurve PolesCount=4 KnotsCount=2 Degree=3 IsPeriodic=0
    g53: BSplineCurve PolesCount=2 KnotsCount=2 Degree=1 IsPeriodic=0
    g54: BSplineCurve PolesCount=2 KnotsCount=2 Degree=1 IsPeriodic=0
    g55: BSplineCurve PolesCount=2 KnotsCount=2 Degree=1 IsPeriodic=0
    g56: BSplineCurve PolesCount=4 KnotsCount=2 Degree=3 IsPeriodic=0
    g57: BSplineCurve PolesCount=2 KnotsCount=2 Degree=1 IsPeriodic=0
    g58: BSplineCurve PolesCount=2 KnotsCount=2 Degree=1 IsPeriodic=0
    g59: BSplineCurve PolesCount=4 KnotsCount=2 Degree=3 IsPeriodic=0
    g60: BSplineCurve PolesCount=4 KnotsCount=2 Degree=3 IsPeriodic=0
    g61: BSplineCurve PolesCount=2 KnotsCount=2 Degree=1 IsPeriodic=0
    g62: BSplineCurve PolesCount=2 KnotsCount=2 Degree=1 IsPeriodic=0
    g63: BSplineCurve PolesCount=4 KnotsCount=2 Degree=3 IsPeriodic=0
    g64: BSplineCurve PolesCount=2 KnotsCount=2 Degree=1 IsPeriodic=0
    g65: BSplineCurve PolesCount=4 KnotsCount=2 Degree=3 IsPeriodic=0
    g66: BSplineCurve PolesCount=4 KnotsCount=2 Degree=3 IsPeriodic=0
    g67: BSplineCurve PolesCount=2 KnotsCount=2 Degree=1 IsPeriodic=0
    g68: BSplineCurve PolesCount=4 KnotsCount=2 Degree=3 IsPeriodic=0
    g69: BSplineCurve PolesCount=2 KnotsCount=2 Degree=1 IsPeriodic=0
    g70: BSplineCurve PolesCount=4 KnotsCount=2 Degree=3 IsPeriodic=0
    g71: BSplineCurve PolesCount=2 KnotsCount=2 Degree=1 IsPeriodic=0
    g72: BSplineCurve PolesCount=4 KnotsCount=2 Degree=3 IsPeriodic=0
    g73: BSplineCurve PolesCount=4 KnotsCount=2 Degree=3 IsPeriodic=0
    g74: BSplineCurve PolesCount=2 KnotsCount=2 Degree=1 IsPeriodic=0
    g75: BSplineCurve PolesCount=2 KnotsCount=2 Degree=1 IsPeriodic=0
    g76: BSplineCurve PolesCount=4 KnotsCount=2 Degree=3 IsPeriodic=0
    g77: BSplineCurve PolesCount=2 KnotsCount=2 Degree=1 IsPeriodic=0
    g78: BSplineCurve PolesCount=4 KnotsCount=2 Degree=3 IsPeriodic=0
    g79: BSplineCurve PolesCount=2 KnotsCount=2 Degree=1 IsPeriodic=0
    g80: BSplineCurve PolesCount=4 KnotsCount=2 Degree=3 IsPeriodic=0
    g81: BSplineCurve PolesCount=4 KnotsCount=2 Degree=3 IsPeriodic=0
    g82: BSplineCurve PolesCount=2 KnotsCount=2 Degree=1 IsPeriodic=0
    g83: BSplineCurve PolesCount=4 KnotsCount=2 Degree=3 IsPeriodic=0
    g84: BSplineCurve PolesCount=2 KnotsCount=2 Degree=1 IsPeriodic=0
    g85: BSplineCurve PolesCount=4 KnotsCount=2 Degree=3 IsPeriodic=0
    g86: BSplineCurve PolesCount=2 KnotsCount=2 Degree=1 IsPeriodic=0
    g87: BSplineCurve PolesCount=4 KnotsCount=2 Degree=3 IsPeriodic=0
    g88: BSplineCurve PolesCount=4 KnotsCount=2 Degree=3 IsPeriodic=0
    g89: BSplineCurve PolesCount=2 KnotsCount=2 Degree=1 IsPeriodic=0
    g90: BSplineCurve PolesCount=4 KnotsCount=2 Degree=3 IsPeriodic=0
    g91: BSplineCurve PolesCount=4 KnotsCount=2 Degree=3 IsPeriodic=0
    g92: BSplineCurve PolesCount=4 KnotsCount=2 Degree=3 IsPeriodic=0
    g93: BSplineCurve PolesCount=2 KnotsCount=2 Degree=1 IsPeriodic=0
    g94: BSplineCurve PolesCount=4 KnotsCount=2 Degree=3 IsPeriodic=0
    g95: BSplineCurve PolesCount=2 KnotsCount=2 Degree=1 IsPeriodic=0
    g96: BSplineCurve PolesCount=4 KnotsCount=2 Degree=3 IsPeriodic=0
    g97: BSplineCurve PolesCount=4 KnotsCount=2 Degree=3 IsPeriodic=0
    g98: BSplineCurve PolesCount=2 KnotsCount=2 Degree=1 IsPeriodic=0
    g99: BSplineCurve PolesCount=4 KnotsCount=2 Degree=3 IsPeriodic=0
    g100: BSplineCurve PolesCount=2 KnotsCount=2 Degree=1 IsPeriodic=0
    g101: BSplineCurve PolesCount=4 KnotsCount=2 Degree=3 IsPeriodic=0
    g102: BSplineCurve PolesCount=2 KnotsCount=2 Degree=1 IsPeriodic=0
    g103: BSplineCurve PolesCount=4 KnotsCount=2 Degree=3 IsPeriodic=0
    g104: BSplineCurve PolesCount=4 KnotsCount=2 Degree=3 IsPeriodic=0
    g105: BSplineCurve PolesCount=2 KnotsCount=2 Degree=1 IsPeriodic=0
    g106: BSplineCurve PolesCount=4 KnotsCount=2 Degree=3 IsPeriodic=0
    g107: BSplineCurve PolesCount=2 KnotsCount=2 Degree=1 IsPeriodic=0
    g108: BSplineCurve PolesCount=4 KnotsCount=2 Degree=3 IsPeriodic=0
    g109: BSplineCurve PolesCount=2 KnotsCount=2 Degree=1 IsPeriodic=0
    g110: BSplineCurve PolesCount=4 KnotsCount=2 Degree=3 IsPeriodic=0
    g111: BSplineCurve PolesCount=2 KnotsCount=2 Degree=1 IsPeriodic=0
    g112: BSplineCurve PolesCount=4 KnotsCount=2 Degree=3 IsPeriodic=0
    g113: BSplineCurve PolesCount=4 KnotsCount=2 Degree=3 IsPeriodic=0
    g114: BSplineCurve PolesCount=2 KnotsCount=2 Degree=1 IsPeriodic=0
    g115: BSplineCurve PolesCount=4 KnotsCount=2 Degree=3 IsPeriodic=0
    g116: BSplineCurve PolesCount=2 KnotsCount=2 Degree=1 IsPeriodic=0
    g117: BSplineCurve PolesCount=2 KnotsCount=2 Degree=1 IsPeriodic=0
    g118: BSplineCurve PolesCount=4 KnotsCount=2 Degree=3 IsPeriodic=0
    g119: BSplineCurve PolesCount=2 KnotsCount=2 Degree=1 IsPeriodic=0
    g120: BSplineCurve PolesCount=4 KnotsCount=2 Degree=3 IsPeriodic=0
    g121: BSplineCurve PolesCount=2 KnotsCount=2 Degree=1 IsPeriodic=0
    g122: BSplineCurve PolesCount=4 KnotsCount=2 Degree=3 IsPeriodic=0
    g123: BSplineCurve PolesCount=2 KnotsCount=2 Degree=1 IsPeriodic=0
    g124: BSplineCurve PolesCount=2 KnotsCount=2 Degree=1 IsPeriodic=0
    g125: BSplineCurve PolesCount=2 KnotsCount=2 Degree=1 IsPeriodic=0
    g126: BSplineCurve PolesCount=4 KnotsCount=2 Degree=3 IsPeriodic=0
    g127: BSplineCurve PolesCount=2 KnotsCount=2 Degree=1 IsPeriodic=0
    g128: BSplineCurve PolesCount=4 KnotsCount=2 Degree=3 IsPeriodic=0
    g129: BSplineCurve PolesCount=2 KnotsCount=2 Degree=1 IsPeriodic=0
    g130: BSplineCurve PolesCount=4 KnotsCount=2 Degree=3 IsPeriodic=0
    g131: BSplineCurve PolesCount=2 KnotsCount=2 Degree=1 IsPeriodic=0
    g132: BSplineCurve PolesCount=4 KnotsCount=2 Degree=3 IsPeriodic=0
    g133: BSplineCurve PolesCount=2 KnotsCount=2 Degree=1 IsPeriodic=0
    g134: BSplineCurve PolesCount=4 KnotsCount=2 Degree=3 IsPeriodic=0
    g135: BSplineCurve PolesCount=2 KnotsCount=2 Degree=1 IsPeriodic=0
    g136: BSplineCurve PolesCount=4 KnotsCount=2 Degree=3 IsPeriodic=0
    g137: BSplineCurve PolesCount=4 KnotsCount=2 Degree=3 IsPeriodic=0
    g138: BSplineCurve PolesCount=2 KnotsCount=2 Degree=1 IsPeriodic=0
    g139: BSplineCurve PolesCount=4 KnotsCount=2 Degree=3 IsPeriodic=0
    g140: BSplineCurve PolesCount=2 KnotsCount=2 Degree=1 IsPeriodic=0
    g141: BSplineCurve PolesCount=2 KnotsCount=2 Degree=1 IsPeriodic=0
    g142: BSplineCurve PolesCount=4 KnotsCount=2 Degree=3 IsPeriodic=0
    g143: BSplineCurve PolesCount=4 KnotsCount=2 Degree=3 IsPeriodic=0
    g144: BSplineCurve PolesCount=2 KnotsCount=2 Degree=1 IsPeriodic=0
    g145: BSplineCurve PolesCount=2 KnotsCount=2 Degree=1 IsPeriodic=0
    g146: BSplineCurve PolesCount=4 KnotsCount=2 Degree=3 IsPeriodic=0
    g147: BSplineCurve PolesCount=2 KnotsCount=2 Degree=1 IsPeriodic=0
    g148: BSplineCurve PolesCount=4 KnotsCount=2 Degree=3 IsPeriodic=0
    g149: BSplineCurve PolesCount=2 KnotsCount=2 Degree=1 IsPeriodic=0
    g150: BSplineCurve PolesCount=4 KnotsCount=2 Degree=3 IsPeriodic=0
    g151: BSplineCurve PolesCount=2 KnotsCount=2 Degree=1 IsPeriodic=0
    g152: BSplineCurve PolesCount=4 KnotsCount=2 Degree=3 IsPeriodic=0
    g153: BSplineCurve PolesCount=4 KnotsCount=2 Degree=3 IsPeriodic=0
    g154: BSplineCurve PolesCount=2 KnotsCount=2 Degree=1 IsPeriodic=0
    g155: BSplineCurve PolesCount=2 KnotsCount=2 Degree=1 IsPeriodic=0
    g156: BSplineCurve PolesCount=2 KnotsCount=2 Degree=1 IsPeriodic=0
    g157: BSplineCurve PolesCount=4 KnotsCount=2 Degree=3 IsPeriodic=0
    g158: BSplineCurve PolesCount=4 KnotsCount=2 Degree=3 IsPeriodic=0
    g159: BSplineCurve PolesCount=4 KnotsCount=2 Degree=3 IsPeriodic=0
    g160: BSplineCurve PolesCount=4 KnotsCount=2 Degree=3 IsPeriodic=0
    g161: BSplineCurve PolesCount=4 KnotsCount=2 Degree=3 IsPeriodic=0
    g162: BSplineCurve PolesCount=4 KnotsCount=2 Degree=3 IsPeriodic=0
    g163: BSplineCurve PolesCount=2 KnotsCount=2 Degree=1 IsPeriodic=0
    g164: BSplineCurve PolesCount=4 KnotsCount=2 Degree=3 IsPeriodic=0
    g165: BSplineCurve PolesCount=2 KnotsCount=2 Degree=1 IsPeriodic=0
    g166: BSplineCurve PolesCount=4 KnotsCount=2 Degree=3 IsPeriodic=0
    g167: BSplineCurve PolesCount=2 KnotsCount=2 Degree=1 IsPeriodic=0
    g168: BSplineCurve PolesCount=2 KnotsCount=2 Degree=1 IsPeriodic=0
    g169: BSplineCurve PolesCount=4 KnotsCount=2 Degree=3 IsPeriodic=0
    g170: BSplineCurve PolesCount=2 KnotsCount=2 Degree=1 IsPeriodic=0
    g171: BSplineCurve PolesCount=4 KnotsCount=2 Degree=3 IsPeriodic=0
    g172: BSplineCurve PolesCount=2 KnotsCount=2 Degree=1 IsPeriodic=0
    g173: BSplineCurve PolesCount=4 KnotsCount=2 Degree=3 IsPeriodic=0
    g174: BSplineCurve PolesCount=2 KnotsCount=2 Degree=1 IsPeriodic=0
    g175: BSplineCurve PolesCount=2 KnotsCount=2 Degree=1 IsPeriodic=0
    g176: BSplineCurve PolesCount=4 KnotsCount=2 Degree=3 IsPeriodic=0
    g177: BSplineCurve PolesCount=4 KnotsCount=2 Degree=3 IsPeriodic=0
    g178: BSplineCurve PolesCount=2 KnotsCount=2 Degree=1 IsPeriodic=0
    g179: BSplineCurve PolesCount=2 KnotsCount=2 Degree=1 IsPeriodic=0
    g180: BSplineCurve PolesCount=4 KnotsCount=2 Degree=3 IsPeriodic=0
    g181: BSplineCurve PolesCount=2 KnotsCount=2 Degree=1 IsPeriodic=0
    g182: BSplineCurve PolesCount=4 KnotsCount=2 Degree=3 IsPeriodic=0
    g183: BSplineCurve PolesCount=4 KnotsCount=2 Degree=3 IsPeriodic=0
    g184: BSplineCurve PolesCount=2 KnotsCount=2 Degree=1 IsPeriodic=0
    g185: BSplineCurve PolesCount=4 KnotsCount=2 Degree=3 IsPeriodic=0
    g186: BSplineCurve PolesCount=2 KnotsCount=2 Degree=1 IsPeriodic=0
    g187: BSplineCurve PolesCount=4 KnotsCount=2 Degree=3 IsPeriodic=0
    g188: BSplineCurve PolesCount=2 KnotsCount=2 Degree=1 IsPeriodic=0
    g189: BSplineCurve PolesCount=4 KnotsCount=2 Degree=3 IsPeriodic=0
    g190: BSplineCurve PolesCount=4 KnotsCount=2 Degree=3 IsPeriodic=0
    g191: BSplineCurve PolesCount=2 KnotsCount=2 Degree=1 IsPeriodic=0
    g192: BSplineCurve PolesCount=4 KnotsCount=2 Degree=3 IsPeriodic=0
    g193: BSplineCurve PolesCount=4 KnotsCount=2 Degree=3 IsPeriodic=0
    g194: BSplineCurve PolesCount=2 KnotsCount=2 Degree=1 IsPeriodic=0
    g195: BSplineCurve PolesCount=4 KnotsCount=2 Degree=3 IsPeriodic=0
    g196: BSplineCurve PolesCount=2 KnotsCount=2 Degree=1 IsPeriodic=0
    g197: BSplineCurve PolesCount=4 KnotsCount=2 Degree=3 IsPeriodic=0
    g198: BSplineCurve PolesCount=2 KnotsCount=2 Degree=1 IsPeriodic=0
    g199: BSplineCurve PolesCount=4 KnotsCount=2 Degree=3 IsPeriodic=0
    g200: BSplineCurve PolesCount=4 KnotsCount=2 Degree=3 IsPeriodic=0
    g201: BSplineCurve PolesCount=2 KnotsCount=2 Degree=1 IsPeriodic=0
    g202: BSplineCurve PolesCount=4 KnotsCount=2 Degree=3 IsPeriodic=0
    g203: BSplineCurve PolesCount=2 KnotsCount=2 Degree=1 IsPeriodic=0
    g204: BSplineCurve PolesCount=4 KnotsCount=2 Degree=3 IsPeriodic=0
    g205: BSplineCurve PolesCount=2 KnotsCount=2 Degree=1 IsPeriodic=0
    g206: BSplineCurve PolesCount=4 KnotsCount=2 Degree=3 IsPeriodic=0
    g207: BSplineCurve PolesCount=2 KnotsCount=2 Degree=1 IsPeriodic=0
    g208: BSplineCurve PolesCount=2 KnotsCount=2 Degree=1 IsPeriodic=0
    g209: BSplineCurve PolesCount=4 KnotsCount=2 Degree=3 IsPeriodic=0
    g210: BSplineCurve PolesCount=4 KnotsCount=2 Degree=3 IsPeriodic=0
    g211: BSplineCurve PolesCount=2 KnotsCount=2 Degree=1 IsPeriodic=0
    g212: BSplineCurve PolesCount=2 KnotsCount=2 Degree=1 IsPeriodic=0
    g213: BSplineCurve PolesCount=4 KnotsCount=2 Degree=3 IsPeriodic=0
    g214: BSplineCurve PolesCount=2 KnotsCount=2 Degree=1 IsPeriodic=0
    g215: BSplineCurve PolesCount=4 KnotsCount=2 Degree=3 IsPeriodic=0
    g216: BSplineCurve PolesCount=4 KnotsCount=2 Degree=3 IsPeriodic=0
    g217: BSplineCurve PolesCount=2 KnotsCount=2 Degree=1 IsPeriodic=0
    g218: BSplineCurve PolesCount=4 KnotsCount=2 Degree=3 IsPeriodic=0
    g219: BSplineCurve PolesCount=2 KnotsCount=2 Degree=1 IsPeriodic=0
    g220: BSplineCurve PolesCount=4 KnotsCount=2 Degree=3 IsPeriodic=0
    g221: BSplineCurve PolesCount=2 KnotsCount=2 Degree=1 IsPeriodic=0
    g222: BSplineCurve PolesCount=4 KnotsCount=2 Degree=3 IsPeriodic=0
    g223: BSplineCurve PolesCount=4 KnotsCount=2 Degree=3 IsPeriodic=0
    g224: BSplineCurve PolesCount=2 KnotsCount=2 Degree=1 IsPeriodic=0
  constraints (225):
    c: Coincident(g0,g1)
    c: Coincident(g1,g2)
    c: Coincident(g2,g3)
    c: Coincident(g3,g4)
    c: Coincident(g4,g5)
    c: Coincident(g5,g6)
    c: Coincident(g6,g7)
    c: Coincident(g7,g8)
    c: Coincident(g8,g9)
    c: Coincident(g9,g10)
    c: Coincident(g10,g11)
    c: Coincident(g11,g12)
    c: Coincident(g12,g13)
    c: Coincident(g13,g14)
    c: Coincident(g14,g15)
    c: Coincident(g15,g16)
    c: Coincident(g16,g17)
    c: Coincident(g17,g18)
    c: Coincident(g18,g19)
    c: Coincident(g19,g20)
    c: Coincident(g20,g21)
    c: Coincident(g21,g22)
    c: Coincident(g22,g23)
    c: Coincident(g23,g0)
    c: Coincident(g24,g25)
    c: Coincident(g25,g26)
    c: Coincident(g26,g27)
    c: Coincident(g27,g28)
    c: Coincident(g28,g29)
    c: Coincident(g29,g30)
    c: Coincident(g30,g31)
    c: Coincident(g31,g32)
    c: Coincident(g32,g33)
    c: Coincident(g33,g34)
    c: Coincident(g34,g35)
    c: Coincident(g35,g24)
    c: Coincident(g36,g37)
    c: Coincident(g37,g38)
    c: Coincident(g38,g39)
    c: Coincident(g39,g40)
    c: Coincident(g40,g41)
    c: Coincident(g41,g36)
    c: Coincident(g42,g43)
    c: Coincident(g43,g44)
    c: Coincident(g44,g45)
    c: Coincident(g45,g46)
    c: Coincident(g46,g47)
    c: Coincident(g47,g48)
    c: Coincident(g48,g49)
    c: Coincident(g49,g42)
    c: Coincident(g50,g51)
    c: Coincident(g51,g52)
    c: Coincident(g52,g53)
    c: Coincident(g53,g54)
    c: Coincident(g54,g55)
    c: Coincident(g55,g50)
    c: Coincident(g56,g57)
    c: Coincident(g57,g58)
    c: Coincident(g58,g59)
    c: Coincident(g59,g60)
    c: Coincident(g60,g61)
    c: Coincident(g61,g62)
    c: Coincident(g62,g63)
    c: Coincident(g63,g64)
    c: Coincident(g64,g65)
    c: Coincident(g65,g66)
    c: Coincident(g66,g67)
    c: Coincident(g67,g68)
    c: Coincident(g68,g69)
    c: Coincident(g69,g70)
    c: Coincident(g70,g71)
    c: Coincident(g71,g72)
    c: Coincident(g72,g73)
    c: Coincident(g73,g74)
    c: Coincident(g74,g56)
    c: Coincident(g75,g76)
    c: Coincident(g76,g77)
    c: Coincident(g77,g78)
    c: Coincident(g78,g79)
    c: Coincident(g79,g80)
    c: Coincident(g80,g81)
    c: Coincident(g81,g82)
    c: Coincident(g82,g83)
    c: Coincident(g83,g84)
    c: Coincident(g84,g85)
    c: Coincident(g85,g86)
    c: Coincident(g86,g87)
    c: Coincident(g87,g88)
    c: Coincident(g88,g89)
    c: Coincident(g89,g90)
    c: Coincident(g90,g91)
    c: Coincident(g91,g75)
    c: Coincident(g92,g93)
    c: Coincident(g93,g94)
    c: Coincident(g94,g95)
    c: Coincident(g95,g96)
    c: Coincident(g96,g97)
    c: Coincident(g97,g98)
    c: Coincident(g98,g99)
    c: Coincident(g99,g100)
    c: Coincident(g100,g101)
    c: Coincident(g101,g102)
    c: Coincident(g102,g103)
    c: Coincident(g103,g104)
    c: Coincident(g104,g105)
    c: Coincident(g105,g92)
    c: Coincident(g106,g107)
    c: Coincident(g107,g108)
    c: Coincident(g108,g109)
    c: Coincident(g109,g110)
    c: Coincident(g110,g111)
    c: Coincident(g111,g112)
    c: Coincident(g112,g113)
    c: Coincident(g113,g114)
    c: Coincident(g114,g115)
    c: Coincident(g115,g116)
    c: Coincident(g116,g106)
    c: Coincident(g117,g118)
    c: Coincident(g118,g119)
    c: Coincident(g119,g120)
    c: Coincident(g120,g121)
    c: Coincident(g121,g122)
    c: Coincident(g122,g123)
    c: Coincident(g123,g117)
    c: Coincident(g124,g125)
    c: Coincident(g125,g126)
    c: Coincident(g126,g127)
    c: Coincident(g127,g128)
    c: Coincident(g128,g129)
    c: Coincident(g129,g124)
    c: Coincident(g130,g131)
    c: Coincident(g131,g132)
    c: Coincident(g132,g133)
    c: Coincident(g133,g134)
    c: Coincident(g134,g135)
    c: Coincident(g135,g136)
    c: Coincident(g136,g137)
    c: Coincident(g137,g138)
    c: Coincident(g138,g139)
    c: Coincident(g139,g140)
    c: Coincident(g140,g141)
    c: Coincident(g141,g142)
    c: Coincident(g142,g143)
    c: Coincident(g143,g144)
    c: Coincident(g144,g145)
    c: Coincident(g145,g146)
    c: Coincident(g146,g147)
    c: Coincident(g147,g148)
    c: Coincident(g148,g130)
    c: Coincident(g149,g150)
    c: Coincident(g150,g151)
    c: Coincident(g151,g152)
    c: Coincident(g152,g153)
    c: Coincident(g153,g154)
    c: Coincident(g154,g155)
    c: Coincident(g155,g156)
    c: Coincident(g156,g157)
    c: Coincident(g157,g158)
    c: Coincident(g158,g159)
    c: Coincident(g159,g160)
    c: Coincident(g160,g161)
    c: Coincident(g161,g162)
    c: Coincident(g162,g163)
    c: Coincident(g163,g164)
    c: Coincident(g164,g165)
    c: Coincident(g165,g149)
    c: Coincident(g166,g167)
    c: Coincident(g167,g168)
    c: Coincident(g168,g169)
    c: Coincident(g169,g170)
    c: Coincident(g170,g171)
    c: Coincident(g171,g172)
    c: Coincident(g172,g166)
    c: Coincident(g173,g174)
    c: Coincident(g174,g175)
    c: Coincident(g175,g176)
    c: Coincident(g176,g177)
    c: Coincident(g177,g178)
    c: Coincident(g178,g179)
    c: Coincident(g179,g180)
    c: Coincident(g180,g181)
    c: Coincident(g181,g182)
    c: Coincident(g182,g183)
    c: Coincident(g183,g184)
    c: Coincident(g184,g185)
    c: Coincident(g185,g186)
    c: Coincident(g186,g187)
    c: Coincident(g187,g188)
    c: Coincident(g188,g189)
    c: Coincident(g189,g190)
    c: Coincident(g190,g191)
    c: Coincident(g191,g173)
    c: Coincident(g192,g193)
    c: Coincident(g193,g194)
    c: Coincident(g194,g195)
    c: Coincident(g195,g196)
    c: Coincident(g196,g197)
    c: Coincident(g197,g198)
    c: Coincident(g198,g199)
    c: Coincident(g199,g200)
    c: Coincident(g200,g201)
    c: Coincident(g201,g202)
    c: Coincident(g202,g203)
    c: Coincident(g203,g204)
    c: Coincident(g204,g205)
    c: Coincident(g205,g192)
    c: Coincident(g206,g207)
    c: Coincident(g207,g208)
    c: Coincident(g208,g209)
    c: Coincident(g209,g210)
    c: Coincident(g210,g211)
    c: Coincident(g211,g212)
    c: Coincident(g212,g213)
    c: Coincident(g213,g214)
    c: Coincident(g214,g215)
    c: Coincident(g215,g216)
    c: Coincident(g216,g217)
    c: Coincident(g217,g218)
    c: Coincident(g218,g219)
    c: Coincident(g219,g220)
    c: Coincident(g220,g221)
    c: Coincident(g221,g222)
    c: Coincident(g222,g223)
    c: Coincident(g223,g224)
    c: Coincident(g224,g206)
FEATURE [PartDesign::Pocket] Pocket021
  BaseFeature = -> Pocket020
  Direction = (-1e-16,-1,0)
  Length = 0.4
  Length2 = 5
  Profile = -> Sketch041
  ReferenceAxis = -> Sketch041 [N_Axis]
  Type = 0
FEATURE [Sketcher::SketchObject] Sketch042
  FullyConstrained = true
  MapMode = 5
  Placement = pos=(0,0,0) rot=(0.57735,0.57735,0.57735;2.0944rad)
  Support = -> [YZ_Plane]
  expr: Constraints[22] = 5.497 / 2
  expr: Constraints[23] = 6.322 / 2
  sketch-geometry (9):
    g0: LineSegment StartX=2.7485 StartY=0.47625 StartZ=0 EndX=3.161 EndY=0.079375 EndZ=0
    g1: LineSegment StartX=2.7485 StartY=-0.47625 StartZ=0 EndX=2.7485 EndY=-0.635 EndZ=0
    g2: LineSegment StartX=2.7485 StartY=-0.635 StartZ=0 EndX=0 EndY=-0.635 EndZ=0
    g3: LineSegment StartX=0 StartY=-0.635 StartZ=0 EndX=0 EndY=0.635 EndZ=0
    g4: LineSegment StartX=0 StartY=0.635 StartZ=0 EndX=2.7485 EndY=0.635 EndZ=0
    g5: LineSegment StartX=2.7485 StartY=0.635 StartZ=0 EndX=2.7485 EndY=0.47625 EndZ=0
    g6: LineSegment StartX=3.161 StartY=0.079375 StartZ=0 EndX=3.161 EndY=-0.079375 EndZ=0
    g7: LineSegment StartX=3.161 StartY=-0.079375 StartZ=0 EndX=2.7485 EndY=-0.47625 EndZ=0
    g8: LineSegment StartX=2.5835 StartY=-0.635 StartZ=0 EndX=3.2435 EndY=0 EndZ=0
  constraints (26):
    c: Vertical(g1)
    c: Coincident(g1,g2)
    c: PointOnObject(g2,g-2)
    c: Horizontal(g2)
    c: Coincident(g2,g3)
    c: Coincident(g3,g4)
    c: Horizontal(g4)
    c: Coincident(g4,g5)
    c: Coincident(g5,g0)
    c: Vertical(g5)
    c: Coincident(g0,g6)
    c: Coincident(g7,g1)
    c: Distance(g3) = 1.27
    c: Symmetric(g6,g0,g-1)
    c: Symmetric(g3,g2,g-1)
    c: Equal(g1,g5)
    c: Vertical(g1,g0)
    c: PointOnObject(g1,g8)
    c: PointOnObject(g8,g2)
    c: Coincident(g6,g7)
    c: PointOnObject(g6,g8)
    c: PointOnObject(g8,g-1)
    c: Distance(g1,g2) = 2.7485
    c: Distance(g6,g3) = 3.161
    c: Distance(g8,g1) = 0.165
    c: Distance(g8,g6) = 0.0825
FEATURE [PartDesign::AdditiveHelix] AdditiveHelix
  Angle = 0
  Axis = (-2e-16,3e-16,1)
  Base = (0,0,0)
  Growth = 0
  HasBeenEdited = true
  Height = 25
  LeftHanded = false
  Mode = 0
  Outside = false
  Pitch = 1.27
  Placement = pos=(0,0,0) rot=(0.57735,0.57735,0.57735;2.0944rad)
  Profile = -> Sketch042
  ReferenceAxis = -> Sketch042 [V_Axis]
  Turns = 19.685
FEATURE [PartDesign::Body] Body  label="UNC_1/4_Outer_Thread"
  Group = -> [Sketch042,AdditiveHelix]
  Origin = -> Origin
  Placement = pos=(0,0,-53) rot=(0,0,1;0rad)
  Tip = -> AdditiveHelix
FEATURE [Sketcher::SketchObject] Sketch043  label="Number_1"
  FullyConstrained = false
  Placement = pos=(-27,-35.1,-200) rot=(1,0,0;1.5708rad)
  expr: .Placement.Base.y = -Spreadsheet.depth / 2
  sketch-geometry (17):
    g0: LineSegment StartX=1.44828 StartY=0 StartZ=0 EndX=1.44828 EndY=2.06897 EndZ=0
    g1: LineSegment StartX=11.0754 StartY=0 StartZ=0 EndX=1.44828 EndY=0 EndZ=0
    g2: LineSegment StartX=11.0754 StartY=2.06897 StartZ=0 EndX=11.0754 EndY=0 EndZ=0
    g3: LineSegment StartX=7.94612 StartY=2.06897 StartZ=0 EndX=11.0754 EndY=2.06897 EndZ=0
    g4: LineSegment StartX=7.94612 StartY=13.2414 StartZ=0 EndX=7.94612 EndY=2.06897 EndZ=0
    g5: LineSegment StartX=5.36638 StartY=13.2414 StartZ=0 EndX=7.94612 EndY=13.2414 EndZ=0
    g6: BSplineCurve PolesCount=3 KnotsCount=2 Degree=2 IsPeriodic=0
    g7: BSplineCurve PolesCount=3 KnotsCount=2 Degree=2 IsPeriodic=0
    g8: BSplineCurve PolesCount=3 KnotsCount=2 Degree=2 IsPeriodic=0
    g9: BSplineCurve PolesCount=3 KnotsCount=2 Degree=2 IsPeriodic=0
    g10: LineSegment StartX=1.33836 StartY=9.10345 StartZ=0 EndX=1.33836 EndY=11.1724 EndZ=0
    g11: BSplineCurve PolesCount=3 KnotsCount=2 Degree=2 IsPeriodic=0
    g12: BSplineCurve PolesCount=3 KnotsCount=2 Degree=2 IsPeriodic=0
    g13: BSplineCurve PolesCount=3 KnotsCount=2 Degree=2 IsPeriodic=0
    g14: BSplineCurve PolesCount=3 KnotsCount=2 Degree=2 IsPeriodic=0
    g15: LineSegment StartX=5.21767 StartY=2.06897 StartZ=0 EndX=5.21767 EndY=10.9138 EndZ=0
    g16: LineSegment StartX=1.44828 StartY=2.06897 StartZ=0 EndX=5.21767 EndY=2.06897 EndZ=0
  constraints (26):
    c: Vertical(g0)
    c: Coincident(g0,g1)
    c: Horizontal(g1)
    c: Coincident(g1,g2)
    c: Vertical(g2)
    c: Coincident(g2,g3)
    c: Horizontal(g3)
    c: Coincident(g3,g4)
    c: Vertical(g4)
    c: Coincident(g4,g5)
    c: Horizontal(g5)
    c: Coincident(g5,g6)
    c: Coincident(g6,g7)
    c: Coincident(g7,g8)
    c: Coincident(g8,g9)
    c: Coincident(g9,g10)
    c: Vertical(g10)
    c: Coincident(g10,g11)
    c: Coincident(g11,g12)
    c: Coincident(g12,g13)
    c: Coincident(g13,g14)
    c: Coincident(g14,g15)
    c: Vertical(g15)
    c: Coincident(g15,g16)
    c: Horizontal(g16)
    c: Coincident(g16,g0)
FEATURE [PartDesign::Pocket] Pocket022  label="Num1"
  BaseFeature = -> Pocket021
  Direction = (0,1,-2e-16)
  Length = 0.4
  Length2 = 5
  Profile = -> Sketch043
  ReferenceAxis = -> Sketch043 [N_Axis]
  Type = 0
FEATURE [Part::Part2DObjectPython] ShapeString  label="Number"  # Draft 2D object (typed FeaturePython)
  FontFile = <userpath>/projects/TallyLight/cad/LiberationMono-Bold.ttf
  MakeFace = true
  Placement = pos=(0,0,0) rot=(1,0,0;1.5708rad)
  Size = 15
  String = 5
  Tracking = 0
FEATURE [Sketcher::SketchObject] Sketch044  label="Number_2"
  FullyConstrained = false
  Placement = pos=(-27,-35.1,-200) rot=(1,0,0;1.5708rad)
  expr: .Placement.Base.y = -Spreadsheet.depth / 2
  sketch-geometry (31):
    g0: LineSegment StartX=1.19612 StartY=0 StartZ=0 EndX=1.19612 EndY=1.71983 EndZ=0
    g1: LineSegment StartX=10.7586 StartY=0 StartZ=0 EndX=1.19612 EndY=0 EndZ=0
    g2: LineSegment StartX=10.7586 StartY=2.06897 StartZ=0 EndX=10.7586 EndY=0 EndZ=0
    g3: LineSegment StartX=4.41595 StartY=2.06897 StartZ=0 EndX=10.7586 EndY=2.06897 EndZ=0
    g4: BSplineCurve PolesCount=3 KnotsCount=2 Degree=2 IsPeriodic=0
    g5: BSplineCurve PolesCount=3 KnotsCount=2 Degree=2 IsPeriodic=0
    g6: BSplineCurve PolesCount=3 KnotsCount=2 Degree=2 IsPeriodic=0
    g7: BSplineCurve PolesCount=3 KnotsCount=2 Degree=2 IsPeriodic=0
    g8: BSplineCurve PolesCount=3 KnotsCount=2 Degree=2 IsPeriodic=0
    g9: BSplineCurve PolesCount=3 KnotsCount=2 Degree=2 IsPeriodic=0
    g10: BSplineCurve PolesCount=3 KnotsCount=2 Degree=2 IsPeriodic=0
    g11: BSplineCurve PolesCount=3 KnotsCount=2 Degree=2 IsPeriodic=0
    g12: BSplineCurve PolesCount=3 KnotsCount=2 Degree=2 IsPeriodic=0
    g13: BSplineCurve PolesCount=3 KnotsCount=2 Degree=2 IsPeriodic=0
    g14: BSplineCurve PolesCount=3 KnotsCount=2 Degree=2 IsPeriodic=0
    g15: BSplineCurve PolesCount=3 KnotsCount=2 Degree=2 IsPeriodic=0
    g16: BSplineCurve PolesCount=3 KnotsCount=2 Degree=2 IsPeriodic=0
    g17: BSplineCurve PolesCount=3 KnotsCount=2 Degree=2 IsPeriodic=0
    g18: LineSegment StartX=4.05388 StartY=9.10345 StartZ=0 EndX=1.3125 EndY=9.25862 EndZ=0
    g19: BSplineCurve PolesCount=3 KnotsCount=2 Degree=2 IsPeriodic=0
    g20: BSplineCurve PolesCount=3 KnotsCount=2 Degree=2 IsPeriodic=0
    g21: BSplineCurve PolesCount=3 KnotsCount=2 Degree=2 IsPeriodic=0
    g22: BSplineCurve PolesCount=3 KnotsCount=2 Degree=2 IsPeriodic=0
    g23: BSplineCurve PolesCount=3 KnotsCount=2 Degree=2 IsPeriodic=0
    g24: BSplineCurve PolesCount=3 KnotsCount=2 Degree=2 IsPeriodic=0
    g25: BSplineCurve PolesCount=3 KnotsCount=2 Degree=2 IsPeriodic=0
    g26: BSplineCurve PolesCount=3 KnotsCount=2 Degree=2 IsPeriodic=0
    g27: BSplineCurve PolesCount=3 KnotsCount=2 Degree=2 IsPeriodic=0
    g28: BSplineCurve PolesCount=3 KnotsCount=2 Degree=2 IsPeriodic=0
    g29: BSplineCurve PolesCount=3 KnotsCount=2 Degree=2 IsPeriodic=0
    g30: BSplineCurve PolesCount=3 KnotsCount=2 Degree=2 IsPeriodic=0
  constraints (35):
    c: Vertical(g0)
    c: Coincident(g0,g1)
    c: Horizontal(g1)
    c: Coincident(g1,g2)
    c: Vertical(g2)
    c: Coincident(g2,g3)
    c: Horizontal(g3)
    c: Coincident(g3,g4)
    c: Coincident(g4,g5)
    c: Coincident(g5,g6)
    c: Coincident(g6,g7)
    c: Coincident(g7,g8)
    c: Coincident(g8,g9)
    c: Coincident(g9,g10)
    c: Coincident(g10,g11)
    c: Coincident(g11,g12)
    c: Coincident(g12,g13)
    c: Coincident(g13,g14)
    c: Coincident(g14,g15)
    c: Coincident(g15,g16)
    c: Coincident(g16,g17)
    c: Coincident(g17,g18)
    c: Coincident(g18,g19)
    c: Coincident(g19,g20)
    c: Coincident(g20,g21)
    c: Coincident(g21,g22)
    c: Coincident(g22,g23)
    c: Coincident(g23,g24)
    c: Coincident(g24,g25)
    c: Coincident(g25,g26)
    c: Coincident(g26,g27)
    c: Coincident(g27,g28)
    c: Coincident(g28,g29)
    c: Coincident(g29,g30)
    c: Coincident(g30,g0)
FEATURE [PartDesign::Pocket] Pocket023  label="Num2"
  BaseFeature = -> Pocket022
  Direction = (0,1,-2e-16)
  Length = 0.4
  Length2 = 5
  Profile = -> Sketch044
  ReferenceAxis = -> Sketch044 [N_Axis]
  Type = 0
FEATURE [Sketcher::SketchObject] Sketch045  label="Number_3"
  FullyConstrained = false
  Placement = pos=(-27,-35.1,-200) rot=(1,0,0;1.5708rad)
  expr: .Placement.Base.y = -Spreadsheet.depth / 2
  sketch-geometry (52):
    g0: BSplineCurve PolesCount=3 KnotsCount=2 Degree=2 IsPeriodic=0
    g1: BSplineCurve PolesCount=3 KnotsCount=2 Degree=2 IsPeriodic=0
    g2: BSplineCurve PolesCount=3 KnotsCount=2 Degree=2 IsPeriodic=0
    g3: BSplineCurve PolesCount=3 KnotsCount=2 Degree=2 IsPeriodic=0
    g4: BSplineCurve PolesCount=3 KnotsCount=2 Degree=2 IsPeriodic=0
    g5: LineSegment StartX=7.64224 StartY=6.91164 StartZ=0 EndX=7.64224 EndY=6.87284 EndZ=0
    g6: BSplineCurve PolesCount=3 KnotsCount=2 Degree=2 IsPeriodic=0
    g7: BSplineCurve PolesCount=3 KnotsCount=2 Degree=2 IsPeriodic=0
    g8: BSplineCurve PolesCount=3 KnotsCount=2 Degree=2 IsPeriodic=0
    g9: BSplineCurve PolesCount=3 KnotsCount=2 Degree=2 IsPeriodic=0
    g10: BSplineCurve PolesCount=3 KnotsCount=2 Degree=2 IsPeriodic=0
    g11: BSplineCurve PolesCount=3 KnotsCount=2 Degree=2 IsPeriodic=0
    g12: BSplineCurve PolesCount=3 KnotsCount=2 Degree=2 IsPeriodic=0
    g13: BSplineCurve PolesCount=3 KnotsCount=2 Degree=2 IsPeriodic=0
    g14: BSplineCurve PolesCount=3 KnotsCount=2 Degree=2 IsPeriodic=0
    g15: BSplineCurve PolesCount=3 KnotsCount=2 Degree=2 IsPeriodic=0
    g16: BSplineCurve PolesCount=3 KnotsCount=2 Degree=2 IsPeriodic=0
    g17: BSplineCurve PolesCount=3 KnotsCount=2 Degree=2 IsPeriodic=0
    g18: LineSegment StartX=3.85991 StartY=9.51724 StartZ=0 EndX=1.13793 EndY=9.70474 EndZ=0
    g19: BSplineCurve PolesCount=3 KnotsCount=2 Degree=2 IsPeriodic=0
    g20: BSplineCurve PolesCount=3 KnotsCount=2 Degree=2 IsPeriodic=0
    g21: BSplineCurve PolesCount=3 KnotsCount=2 Degree=2 IsPeriodic=0
    g22: BSplineCurve PolesCount=3 KnotsCount=2 Degree=2 IsPeriodic=0
    g23: BSplineCurve PolesCount=3 KnotsCount=2 Degree=2 IsPeriodic=0
    g24: BSplineCurve PolesCount=3 KnotsCount=2 Degree=2 IsPeriodic=0
    g25: BSplineCurve PolesCount=3 KnotsCount=2 Degree=2 IsPeriodic=0
    g26: BSplineCurve PolesCount=3 KnotsCount=2 Degree=2 IsPeriodic=0
    g27: BSplineCurve PolesCount=3 KnotsCount=2 Degree=2 IsPeriodic=0
    g28: BSplineCurve PolesCount=3 KnotsCount=2 Degree=2 IsPeriodic=0
    g29: LineSegment StartX=4.45474 StartY=7.86207 StartZ=0 EndX=5.34698 EndY=7.86207 EndZ=0
    g30: LineSegment StartX=4.45474 StartY=5.7931 StartZ=0 EndX=4.45474 EndY=7.86207 EndZ=0
    g31: LineSegment StartX=5.40517 StartY=5.7931 StartZ=0 EndX=4.45474 EndY=5.7931 EndZ=0
    g32: BSplineCurve PolesCount=3 KnotsCount=2 Degree=2 IsPeriodic=0
    g33: BSplineCurve PolesCount=3 KnotsCount=2 Degree=2 IsPeriodic=0
    g34: BSplineCurve PolesCount=3 KnotsCount=2 Degree=2 IsPeriodic=0
    g35: BSplineCurve PolesCount=3 KnotsCount=2 Degree=2 IsPeriodic=0
    g36: BSplineCurve PolesCount=3 KnotsCount=2 Degree=2 IsPeriodic=0
    g37: BSplineCurve PolesCount=3 KnotsCount=2 Degree=2 IsPeriodic=0
    g38: BSplineCurve PolesCount=3 KnotsCount=2 Degree=2 IsPeriodic=0
    g39: BSplineCurve PolesCount=3 KnotsCount=2 Degree=2 IsPeriodic=0
    g40: BSplineCurve PolesCount=3 KnotsCount=2 Degree=2 IsPeriodic=0
    g41: BSplineCurve PolesCount=3 KnotsCount=2 Degree=2 IsPeriodic=0
    g42: BSplineCurve PolesCount=3 KnotsCount=2 Degree=2 IsPeriodic=0
    g43: BSplineCurve PolesCount=3 KnotsCount=2 Degree=2 IsPeriodic=0
    g44: LineSegment StartX=0.905172 StartY=3.89224 StartZ=0 EndX=3.67888 EndY=4.13793 EndZ=0
    g45: BSplineCurve PolesCount=3 KnotsCount=2 Degree=2 IsPeriodic=0
    g46: BSplineCurve PolesCount=3 KnotsCount=2 Degree=2 IsPeriodic=0
    g47: BSplineCurve PolesCount=3 KnotsCount=2 Degree=2 IsPeriodic=0
    g48: BSplineCurve PolesCount=3 KnotsCount=2 Degree=2 IsPeriodic=0
    g49: BSplineCurve PolesCount=3 KnotsCount=2 Degree=2 IsPeriodic=0
    g50: BSplineCurve PolesCount=3 KnotsCount=2 Degree=2 IsPeriodic=0
    g51: BSplineCurve PolesCount=3 KnotsCount=2 Degree=2 IsPeriodic=0
  constraints (56):
    c: Coincident(g0,g1)
    c: Coincident(g1,g2)
    c: Coincident(g2,g3)
    c: Coincident(g3,g4)
    c: Coincident(g4,g5)
    c: Vertical(g5)
    c: Coincident(g5,g6)
    c: Coincident(g6,g7)
    c: Coincident(g7,g8)
    c: Coincident(g8,g9)
    c: Coincident(g9,g10)
    c: Coincident(g10,g11)
    c: Coincident(g11,g12)
    c: Coincident(g12,g13)
    c: Coincident(g13,g14)
    c: Coincident(g14,g15)
    c: Coincident(g15,g16)
    c: Coincident(g16,g17)
    c: Coincident(g17,g18)
    c: Coincident(g18,g19)
    c: Coincident(g19,g20)
    c: Coincident(g20,g21)
    c: Coincident(g21,g22)
    c: Coincident(g22,g23)
    c: Coincident(g23,g24)
    c: Coincident(g24,g25)
    c: Coincident(g25,g26)
    c: Coincident(g26,g27)
    c: Coincident(g27,g28)
    c: Coincident(g28,g29)
    c: Horizontal(g29)
    c: Coincident(g29,g30)
    c: Vertical(g30)
    c: Coincident(g30,g31)
    c: Horizontal(g31)
    c: Coincident(g31,g32)
    c: Coincident(g32,g33)
    c: Coincident(g33,g34)
    c: Coincident(g34,g35)
    c: Coincident(g35,g36)
    c: Coincident(g36,g37)
    c: Coincident(g37,g38)
    c: Coincident(g38,g39)
    c: Coincident(g39,g40)
    c: Coincident(g40,g41)
    c: Coincident(g41,g42)
    c: Coincident(g42,g43)
    c: Coincident(g43,g44)
    c: Coincident(g44,g45)
    c: Coincident(g45,g46)
    c: Coincident(g46,g47)
    c: Coincident(g47,g48)
    c: Coincident(g48,g49)
    c: Coincident(g49,g50)
    c: Coincident(g50,g51)
    c: Coincident(g51,g0)
FEATURE [Sketcher::SketchObject] Sketch046  label="Number_4"
  FullyConstrained = false
  Placement = pos=(-27,-35.1,-200) rot=(1,0,0;1.5708rad)
  expr: .Placement.Base.y = -Spreadsheet.depth / 2
  sketch-geometry (22):
    g0: LineSegment StartX=9.50431 StartY=2.89655 StartZ=0 EndX=9.50431 EndY=0 EndZ=0
    g1: LineSegment StartX=11.3276 StartY=2.89655 StartZ=0 EndX=9.50431 EndY=2.89655 EndZ=0
    g2: LineSegment StartX=11.3276 StartY=4.96552 StartZ=0 EndX=11.3276 EndY=2.89655 EndZ=0
    g3: LineSegment StartX=9.50431 StartY=4.96552 StartZ=0 EndX=11.3276 EndY=4.96552 EndZ=0
    g4: LineSegment StartX=9.50431 StartY=13.2414 StartZ=0 EndX=9.50431 EndY=4.96552 EndZ=0
    g5: LineSegment StartX=6.45905 StartY=13.2414 StartZ=0 EndX=9.50431 EndY=13.2414 EndZ=0
    g6: LineSegment StartX=0.69181 StartY=4.98491 StartZ=0 EndX=6.45905 EndY=13.2414 EndZ=0
    g7: LineSegment StartX=0.69181 StartY=2.89655 StartZ=0 EndX=0.69181 EndY=4.98491 EndZ=0
    g8: LineSegment StartX=6.90517 StartY=2.89655 StartZ=0 EndX=0.69181 EndY=2.89655 EndZ=0
    g9: LineSegment StartX=6.90517 StartY=0 StartZ=0 EndX=6.90517 EndY=2.89655 EndZ=0
    g10: LineSegment StartX=9.50431 StartY=0 StartZ=0 EndX=6.90517 EndY=0 EndZ=0
    g11: BSplineCurve PolesCount=3 KnotsCount=2 Degree=2 IsPeriodic=0
    g12: LineSegment StartX=6.90517 StartY=4.96552 StartZ=0 EndX=6.90517 EndY=8.95474 EndZ=0
    g13: LineSegment StartX=2.9806 StartY=4.96552 StartZ=0 EndX=6.90517 EndY=4.96552 EndZ=0
    g14: LineSegment StartX=6.08405 StartY=9.30388 StartZ=0 EndX=2.9806 EndY=4.96552 EndZ=0
    g15: BSplineCurve PolesCount=3 KnotsCount=2 Degree=2 IsPeriodic=0
    g16: BSplineCurve PolesCount=3 KnotsCount=2 Degree=2 IsPeriodic=0
    g17: BSplineCurve PolesCount=3 KnotsCount=2 Degree=2 IsPeriodic=0
    g18: BSplineCurve PolesCount=3 KnotsCount=2 Degree=2 IsPeriodic=0
    g19: BSplineCurve PolesCount=3 KnotsCount=2 Degree=2 IsPeriodic=0
    g20: BSplineCurve PolesCount=3 KnotsCount=2 Degree=2 IsPeriodic=0
    g21: BSplineCurve PolesCount=3 KnotsCount=2 Degree=2 IsPeriodic=0
  constraints (34):
    c: Vertical(g0)
    c: Coincident(g0,g1)
    c: Horizontal(g1)
    c: Coincident(g1,g2)
    c: Vertical(g2)
    c: Coincident(g2,g3)
    c: Horizontal(g3)
    c: Coincident(g3,g4)
    c: Vertical(g4)
    c: Coincident(g4,g5)
    c: Horizontal(g5)
    c: Coincident(g5,g6)
    c: Coincident(g6,g7)
    c: Vertical(g7)
    c: Coincident(g7,g8)
    c: Horizontal(g8)
    c: Coincident(g8,g9)
    c: Vertical(g9)
    c: Coincident(g9,g10)
    c: Horizontal(g10)
    c: Coincident(g10,g0)
    c: Coincident(g11,g12)
    c: Vertical(g12)
    c: Coincident(g12,g13)
    c: Horizontal(g13)
    c: Coincident(g13,g14)
    c: Coincident(g14,g15)
    c: Coincident(g15,g16)
    c: Coincident(g16,g17)
    c: Coincident(g17,g18)
    c: Coincident(g18,g19)
    c: Coincident(g19,g20)
    c: Coincident(g20,g21)
    c: Coincident(g21,g11)
FEATURE [Sketcher::SketchObject] Sketch047  label="Number_5"
  FullyConstrained = false
  Placement = pos=(-27,-35.1,-20) rot=(1,0,0;1.5708rad)
  expr: .Placement.Base.y = -Spreadsheet.depth / 2
  sketch-geometry (35):
    g0: BSplineCurve PolesCount=3 KnotsCount=2 Degree=2 IsPeriodic=0
    g1: BSplineCurve PolesCount=3 KnotsCount=2 Degree=2 IsPeriodic=0
    g2: BSplineCurve PolesCount=3 KnotsCount=2 Degree=2 IsPeriodic=0
    g3: BSplineCurve PolesCount=3 KnotsCount=2 Degree=2 IsPeriodic=0
    g4: BSplineCurve PolesCount=3 KnotsCount=2 Degree=2 IsPeriodic=0
    g5: BSplineCurve PolesCount=3 KnotsCount=2 Degree=2 IsPeriodic=0
    g6: BSplineCurve PolesCount=3 KnotsCount=2 Degree=2 IsPeriodic=0
    g7: LineSegment StartX=4.35776 StartY=11.1724 StartZ=0 EndX=4.13147 EndY=8.2306 EndZ=0
    g8: LineSegment StartX=10.0991 StartY=11.1724 StartZ=0 EndX=4.35776 EndY=11.1724 EndZ=0
    g9: LineSegment StartX=10.0991 StartY=13.2414 StartZ=0 EndX=10.0991 EndY=11.1724 EndZ=0
    g10: LineSegment StartX=1.88147 StartY=13.2414 StartZ=0 EndX=10.0991 EndY=13.2414 EndZ=0
    g11: LineSegment StartX=1.40948 StartY=6.2069 StartZ=0 EndX=1.88147 EndY=13.2414 EndZ=0
    g12: LineSegment StartX=4.06681 StartY=6.2069 StartZ=0 EndX=1.40948 EndY=6.2069 EndZ=0
    g13: BSplineCurve PolesCount=3 KnotsCount=2 Degree=2 IsPeriodic=0
    g14: BSplineCurve PolesCount=3 KnotsCount=2 Degree=2 IsPeriodic=0
    g15: BSplineCurve PolesCount=3 KnotsCount=2 Degree=2 IsPeriodic=0
    g16: BSplineCurve PolesCount=3 KnotsCount=2 Degree=2 IsPeriodic=0
    g17: BSplineCurve PolesCount=3 KnotsCount=2 Degree=2 IsPeriodic=0
    g18: BSplineCurve PolesCount=3 KnotsCount=2 Degree=2 IsPeriodic=0
    g19: BSplineCurve PolesCount=3 KnotsCount=2 Degree=2 IsPeriodic=0
    g20: BSplineCurve PolesCount=3 KnotsCount=2 Degree=2 IsPeriodic=0
    g21: BSplineCurve PolesCount=3 KnotsCount=2 Degree=2 IsPeriodic=0
    g22: BSplineCurve PolesCount=3 KnotsCount=2 Degree=2 IsPeriodic=0
    g23: BSplineCurve PolesCount=3 KnotsCount=2 Degree=2 IsPeriodic=0
    g24: BSplineCurve PolesCount=3 KnotsCount=2 Degree=2 IsPeriodic=0
    g25: BSplineCurve PolesCount=3 KnotsCount=2 Degree=2 IsPeriodic=0
    g26: BSplineCurve PolesCount=3 KnotsCount=2 Degree=2 IsPeriodic=0
    g27: LineSegment StartX=1.00862 StartY=3.50431 StartZ=0 EndX=3.73707 EndY=3.72414 EndZ=0
    g28: BSplineCurve PolesCount=3 KnotsCount=2 Degree=2 IsPeriodic=0
    g29: BSplineCurve PolesCount=3 KnotsCount=2 Degree=2 IsPeriodic=0
    g30: BSplineCurve PolesCount=3 KnotsCount=2 Degree=2 IsPeriodic=0
    g31: BSplineCurve PolesCount=3 KnotsCount=2 Degree=2 IsPeriodic=0
    g32: BSplineCurve PolesCount=3 KnotsCount=2 Degree=2 IsPeriodic=0
    g33: BSplineCurve PolesCount=3 KnotsCount=2 Degree=2 IsPeriodic=0
    g34: BSplineCurve PolesCount=3 KnotsCount=2 Degree=2 IsPeriodic=0
  constraints (39):
    c: Coincident(g0,g1)
    c: Coincident(g1,g2)
    c: Coincident(g2,g3)
    c: Coincident(g3,g4)
    c: Coincident(g4,g5)
    c: Coincident(g5,g6)
    c: Coincident(g6,g7)
    c: Coincident(g7,g8)
    c: Horizontal(g8)
    c: Coincident(g8,g9)
    c: Vertical(g9)
    c: Coincident(g9,g10)
    c: Horizontal(g10)
    c: Coincident(g10,g11)
    c: Coincident(g11,g12)
    c: Horizontal(g12)
    c: Coincident(g12,g13)
    c: Coincident(g13,g14)
    c: Coincident(g14,g15)
    c: Coincident(g15,g16)
    c: Coincident(g16,g17)
    c: Coincident(g17,g18)
    c: Coincident(g18,g19)
    c: Coincident(g19,g20)
    c: Coincident(g20,g21)
    c: Coincident(g21,g22)
    c: Coincident(g22,g23)
    c: Coincident(g23,g24)
    c: Coincident(g24,g25)
    c: Coincident(g25,g26)
    c: Coincident(g26,g27)
    c: Coincident(g27,g28)
    c: Coincident(g28,g29)
    c: Coincident(g29,g30)
    c: Coincident(g30,g31)
    c: Coincident(g31,g32)
    c: Coincident(g32,g33)
    c: Coincident(g33,g34)
    c: Coincident(g34,g0)
FEATURE [PartDesign::Pocket] Pocket024  label="Num3"
  BaseFeature = -> Pocket023
  Direction = (0,1,-2e-16)
  Length = 0.5
  Length2 = 5
  Profile = -> Sketch045
  ReferenceAxis = -> Sketch045 [N_Axis]
  Type = 0
FEATURE [PartDesign::Pocket] Pocket025  label="Num4"
  BaseFeature = -> Pocket024
  Direction = (0,1,-2e-16)
  Length = 0.5
  Length2 = 5
  Profile = -> Sketch046
  ReferenceAxis = -> Sketch046 [N_Axis]
  Type = 0
FEATURE [PartDesign::Pocket] Pocket026  label="Num5"
  BaseFeature = -> Pocket025
  Direction = (0,1,-2e-16)
  Length = 0.5
  Length2 = 5
  Profile = -> Sketch047
  ReferenceAxis = -> Sketch047 [N_Axis]
  Type = 0
FEATURE [PartDesign::Body] Body002  label="BackCover"
  Group = -> [Sketch004,Pad003,Pocket,Sketch039,Sketch008,Pad006,MultiTransform004,Sketch009,Mirrored011,Mirrored012,Pocket007,MultiTransform,Pocket010,Mirrored013,Mirrored014,Sketch016,Pocket008,Sketch017,Pocket009,Sketch018,Sketch026,Pad011,Sketch027,Pocket016,Sketch028,Pad012,PolarPattern001,Sketch029,Pocket017,PolarPattern002,Chamfer,Sketch,Pocket019,Sketch040,Pocket020,Sketch041,Pocket021,Sketch043,+9 more]
  Origin = -> Origin002
  Placement = pos=(0,0,-1) rot=(0,0,1;0rad)
  Tip = -> Pocket026
FEATURE [App::Part] Part  label="TallyLight"
  Group = -> [Body001,Body002,Body003,Body007,Body008,Body009,Cut,Body010,Common,Fusion]
  Origin = -> Origin023
